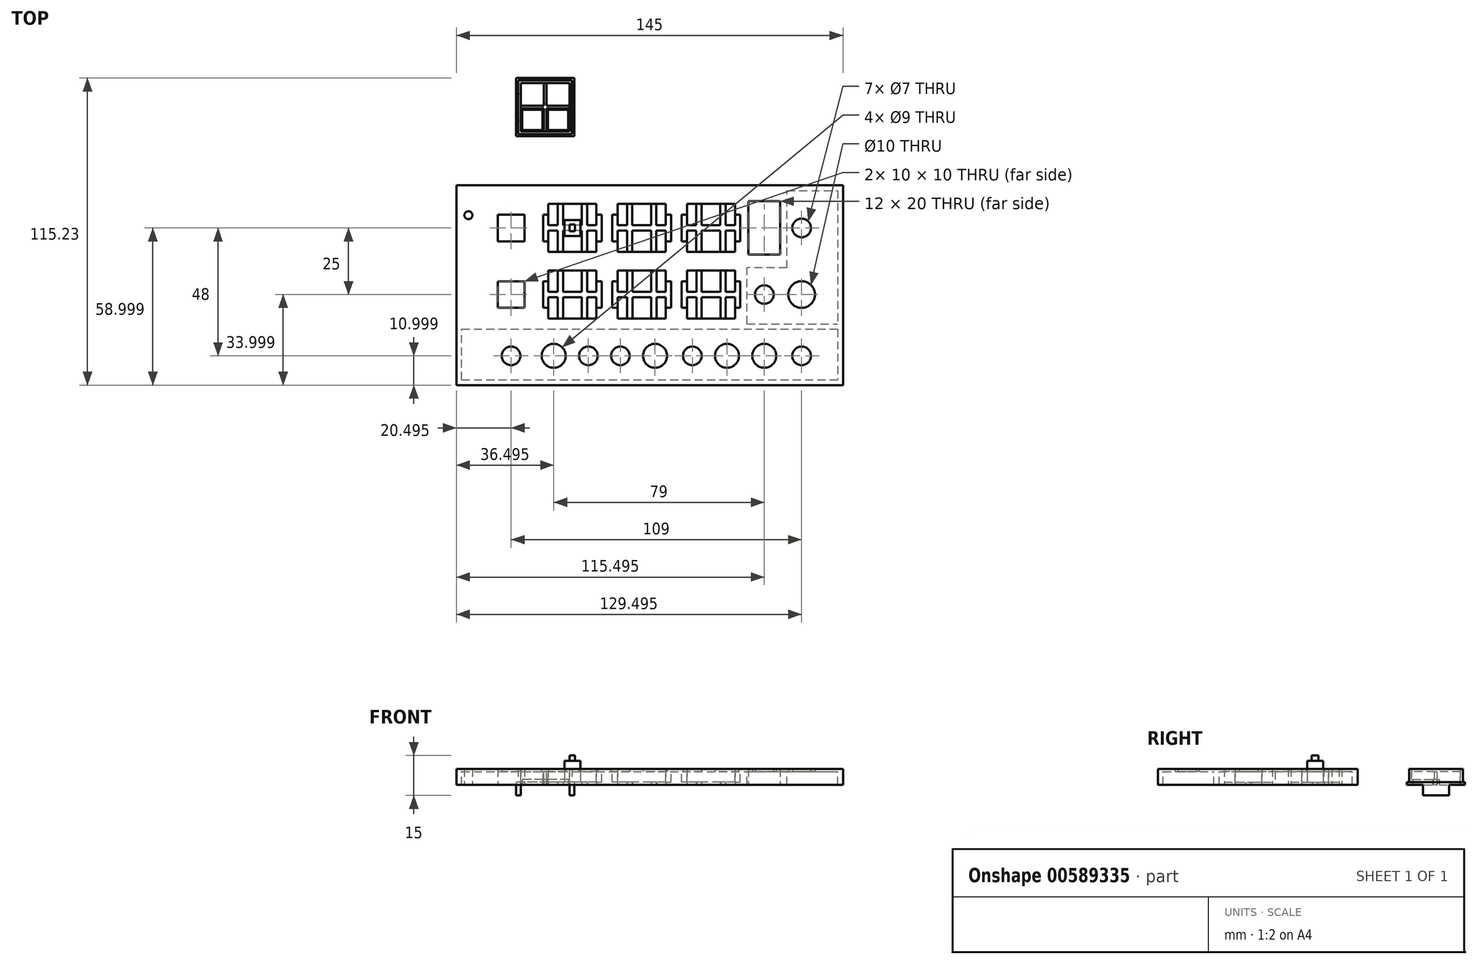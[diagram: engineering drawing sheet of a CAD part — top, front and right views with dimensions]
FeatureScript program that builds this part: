
annotation { "Feature Type Name" : "Feature", "Feature Type Description" : "" }
export const myFeature = defineFeature(function(context is Context, id is Id, definition is map)
    precondition{}
    {
        {
            var Q0;
            Q0=qCreatedBy(makeId("Top.planeOp"),FACE);
            var sketch = newSketch(context, id + "F0", { "sketchPlane" : qUnion([Q0])});
            skLineSegment(sketch, "E0.bottom", {"start": v(-10, -55.04) * mm, "end": v(-155, -55.04) * mm});
            skLineSegment(sketch, "E0.top", {"start": v(-10, 19.96) * mm, "end": v(-155, 19.96) * mm});
            skLineSegment(sketch, "E0.left", {"start": v(-10, -55.04) * mm, "end": v(-10, 19.96) * mm});
            skLineSegment(sketch, "E0.right", {"start": v(-155, -55.04) * mm, "end": v(-155, 19.96) * mm});
            skPoint(sketch, "E0.middle", {"position": v(-82.5, -17.54) * mm});
            skLineSegment(sketch, "E1.bottom", {"start": v(-101.5, -6.04) * mm, "end": v(-121.5, -6.04) * mm, "construction": true});
            skLineSegment(sketch, "E1.top", {"start": v(-101.5, 13.96) * mm, "end": v(-121.5, 13.96) * mm, "construction": true});
            skLineSegment(sketch, "E1.left", {"start": v(-101.5, -6.04) * mm, "end": v(-101.5, 13.96) * mm, "construction": true});
            skLineSegment(sketch, "E1.right", {"start": v(-121.5, -6.04) * mm, "end": v(-121.5, 13.96) * mm, "construction": true});
            skPoint(sketch, "E1.middle", {"position": v(-111.5, 3.96) * mm});
            skLineSegment(sketch, "E2.1.0.0", {"start": v(-95.5, -6.04) * mm, "end": v(-95.5, 13.96) * mm, "construction": true});
            skPoint(sketch, "E2.1.0.1", {"position": v(-85.5, 3.96) * mm});
            skLineSegment(sketch, "E2.1.0.2", {"start": v(-75.5, -6.04) * mm, "end": v(-95.5, -6.04) * mm, "construction": true});
            skLineSegment(sketch, "E2.1.0.3", {"start": v(-75.5, -6.04) * mm, "end": v(-75.5, 13.96) * mm, "construction": true});
            skLineSegment(sketch, "E2.1.0.4", {"start": v(-75.5, 13.96) * mm, "end": v(-95.5, 13.96) * mm, "construction": true});
            skLineSegment(sketch, "E2.2.0.0", {"start": v(-69.5, -6.04) * mm, "end": v(-69.5, 13.96) * mm, "construction": true});
            skPoint(sketch, "E2.2.0.1", {"position": v(-59.5, 3.96) * mm});
            skLineSegment(sketch, "E2.2.0.2", {"start": v(-49.5, -6.04) * mm, "end": v(-69.5, -6.04) * mm, "construction": true});
            skLineSegment(sketch, "E2.2.0.3", {"start": v(-49.5, -6.04) * mm, "end": v(-49.5, 13.96) * mm, "construction": true});
            skLineSegment(sketch, "E2.2.0.4", {"start": v(-49.5, 13.96) * mm, "end": v(-69.5, 13.96) * mm, "construction": true});
            skLineSegment(sketch, "E2.direction1", {"start": v(-121.5, -6.04) * mm, "end": v(-95.5, -6.04) * mm, "construction": true});
            skLineSegment(sketch, "E3.bottom", {"start": v(-101.5, -31.04) * mm, "end": v(-121.5, -31.04) * mm, "construction": true});
            skLineSegment(sketch, "E3.top", {"start": v(-101.5, -11.04) * mm, "end": v(-121.5, -11.04) * mm, "construction": true});
            skLineSegment(sketch, "E3.left", {"start": v(-101.5, -31.04) * mm, "end": v(-101.5, -11.04) * mm, "construction": true});
            skLineSegment(sketch, "E3.right", {"start": v(-121.5, -31.04) * mm, "end": v(-121.5, -11.04) * mm, "construction": true});
            skPoint(sketch, "E3.middle", {"position": v(-111.5, -21.04) * mm});
            skLineSegment(sketch, "E4.1.0.0", {"start": v(-75.5, -31.04) * mm, "end": v(-95.5, -31.04) * mm, "construction": true});
            skLineSegment(sketch, "E4.1.0.1", {"start": v(-75.5, -31.04) * mm, "end": v(-75.5, -11.04) * mm, "construction": true});
            skLineSegment(sketch, "E4.1.0.2", {"start": v(-95.5, -31.04) * mm, "end": v(-95.5, -11.04) * mm, "construction": true});
            skLineSegment(sketch, "E4.1.0.3", {"start": v(-75.5, -11.04) * mm, "end": v(-95.5, -11.04) * mm, "construction": true});
            skPoint(sketch, "E4.1.0.4", {"position": v(-85.5, -21.04) * mm});
            skLineSegment(sketch, "E4.2.0.0", {"start": v(-49.5, -31.04) * mm, "end": v(-69.5, -31.04) * mm, "construction": true});
            skLineSegment(sketch, "E4.2.0.1", {"start": v(-49.5, -31.04) * mm, "end": v(-49.5, -11.04) * mm, "construction": true});
            skLineSegment(sketch, "E4.2.0.2", {"start": v(-69.5, -31.04) * mm, "end": v(-69.5, -11.04) * mm, "construction": true});
            skLineSegment(sketch, "E4.2.0.3", {"start": v(-49.5, -11.04) * mm, "end": v(-69.5, -11.04) * mm, "construction": true});
            skPoint(sketch, "E4.2.0.4", {"position": v(-59.5, -21.04) * mm});
            skLineSegment(sketch, "E4.direction1", {"start": v(-121.5, -31.04) * mm, "end": v(-95.5, -31.04) * mm, "construction": true});
            skCircle(sketch, "E5", {"center": v(-134.5, -44.04) * mm, "radius": 3.5 * mm});
            skCircle(sketch, "E6", {"center": v(-105.5, -44.04) * mm, "radius": 3.5 * mm});
            skCircle(sketch, "E7", {"center": v(-93.5, -44.04) * mm, "radius": 3.5 * mm});
            skLineSegment(sketch, "E8.bottom", {"start": v(-155, 19.96) * mm, "end": v(-147, 19.96) * mm, "construction": true});
            skLineSegment(sketch, "E8.top", {"start": v(-155, -55.04) * mm, "end": v(-147, -55.04) * mm, "construction": true});
            skLineSegment(sketch, "E8.left", {"start": v(-155, 19.96) * mm, "end": v(-155, -55.04) * mm, "construction": true});
            skLineSegment(sketch, "E8.right", {"start": v(-147, 19.96) * mm, "end": v(-147, -55.04) * mm, "construction": true});
            skLineSegment(sketch, "E9.bottom", {"start": v(-10, -55.04) * mm, "end": v(-18, -55.04) * mm, "construction": true});
            skLineSegment(sketch, "E9.top", {"start": v(-10, 19.96) * mm, "end": v(-18, 19.96) * mm, "construction": true});
            skLineSegment(sketch, "E9.left", {"start": v(-10, -55.04) * mm, "end": v(-10, 19.96) * mm, "construction": true});
            skLineSegment(sketch, "E9.right", {"start": v(-18, -55.04) * mm, "end": v(-18, 19.96) * mm, "construction": true});
            skCircle(sketch, "E10", {"center": v(-118.5, -44.04) * mm, "radius": 4.5 * mm});
            skCircle(sketch, "E11", {"center": v(-80.5, -44.04) * mm, "radius": 4.5 * mm});
            skCircle(sketch, "E12", {"center": v(-66.5, -44.04) * mm, "radius": 3.5 * mm});
            skCircle(sketch, "E13", {"center": v(-53.5, -44.04) * mm, "radius": 4.5 * mm});
            skCircle(sketch, "E14", {"center": v(-39.5, -44.04) * mm, "radius": 4.5 * mm});
            skCircle(sketch, "E15", {"center": v(-25.5, -44.04) * mm, "radius": 3.5 * mm});
            skCircle(sketch, "E16", {"center": v(-39.5, -21.04) * mm, "radius": 3.5 * mm});
            skLineSegment(sketch, "E17.bottom", {"start": v(-33.5, -6.04) * mm, "end": v(-45.5, -6.04) * mm});
            skLineSegment(sketch, "E17.top", {"start": v(-33.5, 13.96) * mm, "end": v(-45.5, 13.96) * mm});
            skLineSegment(sketch, "E17.left", {"start": v(-33.5, -6.04) * mm, "end": v(-33.5, 13.96) * mm});
            skLineSegment(sketch, "E17.right", {"start": v(-45.5, -6.04) * mm, "end": v(-45.5, 13.96) * mm});
            skPoint(sketch, "E17.middle", {"position": v(-39.5, 3.96) * mm});
            skCircle(sketch, "E18", {"center": v(-25.5, 3.96) * mm, "radius": 3.5 * mm});
            skCircle(sketch, "E19", {"center": v(-25.5, -21.04) * mm, "radius": 5 * mm});
            skPoint(sketch, "E20.centerSnap0", {"position": v(-121.5, -21.04) * mm});
            skLineSegment(sketch, "E21.bottom", {"start": v(-102.5, -5.04) * mm, "end": v(-120.5, -5.04) * mm});
            skLineSegment(sketch, "E21.top", {"start": v(-102.5, 12.96) * mm, "end": v(-120.5, 12.96) * mm});
            skLineSegment(sketch, "E21.left", {"start": v(-102.5, -5.04) * mm, "end": v(-102.5, 12.96) * mm});
            skLineSegment(sketch, "E21.right", {"start": v(-120.5, -5.04) * mm, "end": v(-120.5, 12.96) * mm});
            skLineSegment(sketch, "E22.bottom", {"start": v(-102.5, -30.04) * mm, "end": v(-120.5, -30.04) * mm});
            skLineSegment(sketch, "E22.top", {"start": v(-102.5, -12.04) * mm, "end": v(-120.5, -12.04) * mm});
            skLineSegment(sketch, "E22.left", {"start": v(-102.5, -30.04) * mm, "end": v(-102.5, -12.04) * mm});
            skLineSegment(sketch, "E22.right", {"start": v(-120.5, -30.04) * mm, "end": v(-120.5, -12.04) * mm});
            skLineSegment(sketch, "E23.bottom", {"start": v(-102.5, 2.96) * mm, "end": v(-106, 2.96) * mm});
            skLineSegment(sketch, "E23.top", {"start": v(-102.5, 4.96) * mm, "end": v(-106, 4.96) * mm});
            skLineSegment(sketch, "E23.left", {"start": v(-102.5, 2.96) * mm, "end": v(-102.5, 4.96) * mm});
            skLineSegment(sketch, "E23.right", {"start": v(-120.5, 2.96) * mm, "end": v(-120.5, 4.96) * mm});
            skLineSegment(sketch, "E24.bottom", {"start": v(-115, -5.04) * mm, "end": v(-117, -5.04) * mm});
            skLineSegment(sketch, "E24.top", {"start": v(-115, 12.96) * mm, "end": v(-117, 12.96) * mm});
            skLineSegment(sketch, "E24.left", {"start": v(-115, -5.04) * mm, "end": v(-115, 2.96) * mm});
            skLineSegment(sketch, "E24.right", {"start": v(-117, -5.04) * mm, "end": v(-117, 2.96) * mm});
            skPoint(sketch, "E24.middle", {"position": v(-116, 3.96) * mm});
            skLineSegment(sketch, "E25.bottom", {"start": v(-106, -5.04) * mm, "end": v(-108, -5.04) * mm});
            skLineSegment(sketch, "E25.top", {"start": v(-106, 12.96) * mm, "end": v(-108, 12.96) * mm});
            skLineSegment(sketch, "E25.left", {"start": v(-106, -5.04) * mm, "end": v(-106, 2.96) * mm});
            skLineSegment(sketch, "E25.right", {"start": v(-108, -5.04) * mm, "end": v(-108, 2.96) * mm});
            skPoint(sketch, "E25.middle", {"position": v(-107, 3.96) * mm});
            skLineSegment(sketch, "E26.trimOffspring", {"start": v(-117, 4.96) * mm, "end": v(-117, 12.96) * mm});
            skLineSegment(sketch, "E27.trimOffspring", {"start": v(-117, 4.96) * mm, "end": v(-120.5, 4.96) * mm});
            skLineSegment(sketch, "E28.trimOffspring", {"start": v(-115, 4.96) * mm, "end": v(-115, 12.96) * mm});
            skLineSegment(sketch, "E29.trimOffspring", {"start": v(-117, 2.96) * mm, "end": v(-120.5, 2.96) * mm});
            skLineSegment(sketch, "E30.trimOffspring", {"start": v(-108, 4.96) * mm, "end": v(-108, 12.96) * mm});
            skLineSegment(sketch, "E31.trimOffspring", {"start": v(-108, 4.96) * mm, "end": v(-115, 4.96) * mm});
            skLineSegment(sketch, "E32.trimOffspring", {"start": v(-106, 4.96) * mm, "end": v(-106, 12.96) * mm});
            skLineSegment(sketch, "E33.trimOffspring", {"start": v(-108, 2.96) * mm, "end": v(-115, 2.96) * mm});
            skLineSegment(sketch, "E34.bottom", {"start": v(-131, -50.54) * mm, "end": v(-138, -50.54) * mm, "construction": true});
            skLineSegment(sketch, "E34.top", {"start": v(-131, -37.54) * mm, "end": v(-138, -37.54) * mm, "construction": true});
            skLineSegment(sketch, "E34.left", {"start": v(-131, -50.54) * mm, "end": v(-131, -37.54) * mm, "construction": true});
            skLineSegment(sketch, "E34.right", {"start": v(-138, -50.54) * mm, "end": v(-138, -37.54) * mm, "construction": true});
            skLineSegment(sketch, "E35.bottom", {"start": v(-102.5, -22.04) * mm, "end": v(-105.98, -22.04) * mm});
            skLineSegment(sketch, "E35.top", {"start": v(-102.5, -20.04) * mm, "end": v(-105.98, -20.04) * mm});
            skLineSegment(sketch, "E35.left", {"start": v(-102.5, -22.04) * mm, "end": v(-102.5, -20.04) * mm});
            skLineSegment(sketch, "E35.right", {"start": v(-120.5, -22.04) * mm, "end": v(-120.5, -20.04) * mm});
            skLineSegment(sketch, "E36.bottom", {"start": v(-114.98, -30.04) * mm, "end": v(-116.98, -30.04) * mm});
            skLineSegment(sketch, "E36.top", {"start": v(-114.98, -12.04) * mm, "end": v(-116.98, -12.04) * mm});
            skLineSegment(sketch, "E36.left", {"start": v(-114.98, -30.04) * mm, "end": v(-114.98, -22.04) * mm});
            skLineSegment(sketch, "E36.right", {"start": v(-116.98, -30.04) * mm, "end": v(-116.98, -22.04) * mm});
            skPoint(sketch, "E36.middle", {"position": v(-115.98, -21.04) * mm});
            skLineSegment(sketch, "E37.bottom", {"start": v(-105.98, -30.04) * mm, "end": v(-107.98, -30.04) * mm});
            skLineSegment(sketch, "E37.top", {"start": v(-105.98, -12.04) * mm, "end": v(-107.98, -12.04) * mm});
            skLineSegment(sketch, "E37.left", {"start": v(-105.98, -30.04) * mm, "end": v(-105.98, -22.04) * mm});
            skLineSegment(sketch, "E37.right", {"start": v(-107.98, -30.04) * mm, "end": v(-107.98, -22.04) * mm});
            skPoint(sketch, "E37.middle", {"position": v(-106.98, -21.04) * mm});
            skLineSegment(sketch, "E38.trimOffspring", {"start": v(-116.98, -20.04) * mm, "end": v(-116.98, -12.04) * mm});
            skLineSegment(sketch, "E39.trimOffspring", {"start": v(-116.98, -20.04) * mm, "end": v(-120.5, -20.04) * mm});
            skLineSegment(sketch, "E40.trimOffspring", {"start": v(-114.98, -20.04) * mm, "end": v(-114.98, -12.04) * mm});
            skLineSegment(sketch, "E41.trimOffspring", {"start": v(-116.98, -22.04) * mm, "end": v(-120.5, -22.04) * mm});
            skLineSegment(sketch, "E42.trimOffspring", {"start": v(-107.98, -20.04) * mm, "end": v(-107.98, -12.04) * mm});
            skLineSegment(sketch, "E43.trimOffspring", {"start": v(-107.98, -20.04) * mm, "end": v(-114.98, -20.04) * mm});
            skLineSegment(sketch, "E44.trimOffspring", {"start": v(-105.98, -20.04) * mm, "end": v(-105.98, -12.04) * mm});
            skLineSegment(sketch, "E45.trimOffspring", {"start": v(-107.98, -22.04) * mm, "end": v(-114.98, -22.04) * mm});
            skLineSegment(sketch, "E46.bottom", {"start": v(-129.5, -1.04) * mm, "end": v(-139.5, -1.04) * mm});
            skLineSegment(sketch, "E46.top", {"start": v(-129.5, 8.96) * mm, "end": v(-139.5, 8.96) * mm});
            skLineSegment(sketch, "E46.left", {"start": v(-129.5, -1.04) * mm, "end": v(-129.5, 8.96) * mm});
            skLineSegment(sketch, "E46.right", {"start": v(-139.5, -1.04) * mm, "end": v(-139.5, 8.96) * mm});
            skPoint(sketch, "E46.middle", {"position": v(-134.5, 3.96) * mm});
            skLineSegment(sketch, "E47.bottom", {"start": v(-129.5, -26.04) * mm, "end": v(-139.5, -26.04) * mm});
            skLineSegment(sketch, "E47.top", {"start": v(-129.5, -16.04) * mm, "end": v(-139.5, -16.04) * mm});
            skLineSegment(sketch, "E47.left", {"start": v(-129.5, -26.04) * mm, "end": v(-129.5, -16.04) * mm});
            skLineSegment(sketch, "E47.right", {"start": v(-139.5, -26.04) * mm, "end": v(-139.5, -16.04) * mm});
            skPoint(sketch, "E47.middle", {"position": v(-134.5, -21.04) * mm});
            skLineSegment(sketch, "E48.1.0.0", {"start": v(-91, 4.96) * mm, "end": v(-91, 12.96) * mm});
            skLineSegment(sketch, "E48.1.0.2", {"start": v(-76.5, -5.04) * mm, "end": v(-76.5, 12.96) * mm});
            skLineSegment(sketch, "E48.1.0.3", {"start": v(-80, -5.04) * mm, "end": v(-80, 2.96) * mm});
            skPoint(sketch, "E48.1.0.4", {"position": v(-90, 3.96) * mm});
            skLineSegment(sketch, "E48.1.0.5", {"start": v(-82, 4.96) * mm, "end": v(-82, 12.96) * mm});
            skLineSegment(sketch, "E48.1.0.6", {"start": v(-80, 4.96) * mm, "end": v(-80, 12.96) * mm});
            skLineSegment(sketch, "E48.1.0.7", {"start": v(-82, 4.96) * mm, "end": v(-89, 4.96) * mm});
            skLineSegment(sketch, "E48.1.0.8", {"start": v(-76.5, 4.96) * mm, "end": v(-80, 4.96) * mm});
            skLineSegment(sketch, "E48.1.0.9", {"start": v(-76.5, 2.96) * mm, "end": v(-80, 2.96) * mm});
            skLineSegment(sketch, "E48.1.0.10", {"start": v(-80, 12.96) * mm, "end": v(-82, 12.96) * mm});
            skPoint(sketch, "E48.1.0.11", {"position": v(-81, 3.96) * mm});
            skLineSegment(sketch, "E48.1.0.12", {"start": v(-91, 4.96) * mm, "end": v(-94.5, 4.96) * mm});
            skLineSegment(sketch, "E48.1.0.13", {"start": v(-91, 2.96) * mm, "end": v(-94.5, 2.96) * mm});
            skLineSegment(sketch, "E48.1.0.14", {"start": v(-89, 4.96) * mm, "end": v(-89, 12.96) * mm});
            skLineSegment(sketch, "E48.1.0.15", {"start": v(-76.5, 12.96) * mm, "end": v(-94.5, 12.96) * mm});
            skLineSegment(sketch, "E48.1.0.16", {"start": v(-91, -5.04) * mm, "end": v(-91, 2.96) * mm});
            skLineSegment(sketch, "E48.1.0.17", {"start": v(-76.5, -5.04) * mm, "end": v(-94.5, -5.04) * mm});
            skLineSegment(sketch, "E48.1.0.18", {"start": v(-89, -5.04) * mm, "end": v(-89, 2.96) * mm});
            skLineSegment(sketch, "E48.1.0.19", {"start": v(-82, -5.04) * mm, "end": v(-82, 2.96) * mm});
            skLineSegment(sketch, "E48.1.0.20", {"start": v(-94.5, -5.04) * mm, "end": v(-94.5, 12.96) * mm});
            skLineSegment(sketch, "E48.1.0.21", {"start": v(-82, 2.96) * mm, "end": v(-89, 2.96) * mm});
            skLineSegment(sketch, "E48.1.0.22", {"start": v(-80, -5.04) * mm, "end": v(-82, -5.04) * mm});
            skLineSegment(sketch, "E48.1.0.23", {"start": v(-76.5, 2.96) * mm, "end": v(-76.5, 4.96) * mm});
            skLineSegment(sketch, "E48.1.0.24", {"start": v(-89, -5.04) * mm, "end": v(-91, -5.04) * mm});
            skLineSegment(sketch, "E48.1.0.25", {"start": v(-94.5, 2.96) * mm, "end": v(-94.5, 4.96) * mm});
            skLineSegment(sketch, "E48.1.0.27", {"start": v(-89, 12.96) * mm, "end": v(-91, 12.96) * mm});
            skLineSegment(sketch, "E48.2.0.0", {"start": v(-65, 4.96) * mm, "end": v(-65, 12.96) * mm});
            skLineSegment(sketch, "E48.2.0.2", {"start": v(-50.5, -5.04) * mm, "end": v(-50.5, 12.96) * mm});
            skLineSegment(sketch, "E48.2.0.3", {"start": v(-54, -5.04) * mm, "end": v(-54, 2.96) * mm});
            skPoint(sketch, "E48.2.0.4", {"position": v(-64, 3.96) * mm});
            skLineSegment(sketch, "E48.2.0.5", {"start": v(-56, 4.96) * mm, "end": v(-56, 12.96) * mm});
            skLineSegment(sketch, "E48.2.0.6", {"start": v(-54, 4.96) * mm, "end": v(-54, 12.96) * mm});
            skLineSegment(sketch, "E48.2.0.7", {"start": v(-56, 4.96) * mm, "end": v(-63, 4.96) * mm});
            skLineSegment(sketch, "E48.2.0.8", {"start": v(-50.5, 4.96) * mm, "end": v(-54, 4.96) * mm});
            skLineSegment(sketch, "E48.2.0.9", {"start": v(-50.5, 2.96) * mm, "end": v(-54, 2.96) * mm});
            skLineSegment(sketch, "E48.2.0.10", {"start": v(-54, 12.96) * mm, "end": v(-56, 12.96) * mm});
            skPoint(sketch, "E48.2.0.11", {"position": v(-55, 3.96) * mm});
            skLineSegment(sketch, "E48.2.0.12", {"start": v(-65, 4.96) * mm, "end": v(-68.5, 4.96) * mm});
            skLineSegment(sketch, "E48.2.0.13", {"start": v(-65, 2.96) * mm, "end": v(-68.5, 2.96) * mm});
            skLineSegment(sketch, "E48.2.0.14", {"start": v(-63, 4.96) * mm, "end": v(-63, 12.96) * mm});
            skLineSegment(sketch, "E48.2.0.15", {"start": v(-50.5, 12.96) * mm, "end": v(-68.5, 12.96) * mm});
            skLineSegment(sketch, "E48.2.0.16", {"start": v(-65, -5.04) * mm, "end": v(-65, 2.96) * mm});
            skLineSegment(sketch, "E48.2.0.17", {"start": v(-50.5, -5.04) * mm, "end": v(-68.5, -5.04) * mm});
            skLineSegment(sketch, "E48.2.0.18", {"start": v(-63, -5.04) * mm, "end": v(-63, 2.96) * mm});
            skLineSegment(sketch, "E48.2.0.19", {"start": v(-56, -5.04) * mm, "end": v(-56, 2.96) * mm});
            skLineSegment(sketch, "E48.2.0.20", {"start": v(-68.5, -5.04) * mm, "end": v(-68.5, 12.96) * mm});
            skLineSegment(sketch, "E48.2.0.21", {"start": v(-56, 2.96) * mm, "end": v(-63, 2.96) * mm});
            skLineSegment(sketch, "E48.2.0.22", {"start": v(-54, -5.04) * mm, "end": v(-56, -5.04) * mm});
            skLineSegment(sketch, "E48.2.0.23", {"start": v(-50.5, 2.96) * mm, "end": v(-50.5, 4.96) * mm});
            skLineSegment(sketch, "E48.2.0.24", {"start": v(-63, -5.04) * mm, "end": v(-65, -5.04) * mm});
            skLineSegment(sketch, "E48.2.0.25", {"start": v(-68.5, 2.96) * mm, "end": v(-68.5, 4.96) * mm});
            skLineSegment(sketch, "E48.2.0.27", {"start": v(-63, 12.96) * mm, "end": v(-65, 12.96) * mm});
            skLineSegment(sketch, "E48.direction1", {"start": v(-120.5, -5.04) * mm, "end": v(-94.5, -5.04) * mm, "construction": true});
            skLineSegment(sketch, "E49.1.0.0", {"start": v(-76.5, -20.04) * mm, "end": v(-79.98, -20.04) * mm});
            skLineSegment(sketch, "E49.1.0.1", {"start": v(-88.98, -20.04) * mm, "end": v(-88.98, -12.04) * mm});
            skLineSegment(sketch, "E49.1.0.2", {"start": v(-81.98, -30.04) * mm, "end": v(-81.98, -22.04) * mm});
            skLineSegment(sketch, "E49.1.0.3", {"start": v(-94.5, -30.04) * mm, "end": v(-94.5, -12.04) * mm});
            skLineSegment(sketch, "E49.1.0.4", {"start": v(-90.98, -30.04) * mm, "end": v(-90.98, -22.04) * mm});
            skLineSegment(sketch, "E49.1.0.5", {"start": v(-76.5, -30.04) * mm, "end": v(-76.5, -12.04) * mm});
            skLineSegment(sketch, "E49.1.0.6", {"start": v(-81.98, -22.04) * mm, "end": v(-88.98, -22.04) * mm});
            skLineSegment(sketch, "E49.1.0.7", {"start": v(-88.98, -30.04) * mm, "end": v(-88.98, -22.04) * mm});
            skLineSegment(sketch, "E49.1.0.9", {"start": v(-79.98, -20.04) * mm, "end": v(-79.98, -12.04) * mm});
            skLineSegment(sketch, "E49.1.0.10", {"start": v(-76.5, -22.04) * mm, "end": v(-79.98, -22.04) * mm});
            skPoint(sketch, "E49.1.0.11", {"position": v(-80.98, -21.04) * mm});
            skLineSegment(sketch, "E49.1.0.12", {"start": v(-90.98, -22.04) * mm, "end": v(-94.5, -22.04) * mm});
            skLineSegment(sketch, "E49.1.0.14", {"start": v(-81.98, -20.04) * mm, "end": v(-88.98, -20.04) * mm});
            skPoint(sketch, "E49.1.0.15", {"position": v(-89.98, -21.04) * mm});
            skLineSegment(sketch, "E49.1.0.16", {"start": v(-79.98, -30.04) * mm, "end": v(-79.98, -22.04) * mm});
            skLineSegment(sketch, "E49.1.0.17", {"start": v(-76.5, -30.04) * mm, "end": v(-94.5, -30.04) * mm});
            skLineSegment(sketch, "E49.1.0.18", {"start": v(-90.98, -20.04) * mm, "end": v(-90.98, -12.04) * mm});
            skLineSegment(sketch, "E49.1.0.19", {"start": v(-81.98, -20.04) * mm, "end": v(-81.98, -12.04) * mm});
            skLineSegment(sketch, "E49.1.0.20", {"start": v(-90.98, -20.04) * mm, "end": v(-94.5, -20.04) * mm});
            skLineSegment(sketch, "E49.1.0.21", {"start": v(-76.5, -12.04) * mm, "end": v(-94.5, -12.04) * mm});
            skLineSegment(sketch, "E49.1.0.22", {"start": v(-88.98, -12.04) * mm, "end": v(-90.98, -12.04) * mm});
            skLineSegment(sketch, "E49.1.0.23", {"start": v(-76.5, -22.04) * mm, "end": v(-76.5, -20.04) * mm});
            skLineSegment(sketch, "E49.1.0.24", {"start": v(-94.5, -22.04) * mm, "end": v(-94.5, -20.04) * mm});
            skLineSegment(sketch, "E49.1.0.26", {"start": v(-94.5, -30.04) * mm, "end": v(-94.5, -12.04) * mm});
            skLineSegment(sketch, "E49.1.0.27", {"start": v(-79.98, -12.04) * mm, "end": v(-81.98, -12.04) * mm});
            skLineSegment(sketch, "E49.1.0.28", {"start": v(-76.5, -30.04) * mm, "end": v(-94.5, -30.04) * mm});
            skLineSegment(sketch, "E49.1.0.29", {"start": v(-76.5, -12.04) * mm, "end": v(-94.5, -12.04) * mm});
            skLineSegment(sketch, "E49.1.0.30", {"start": v(-76.5, -30.04) * mm, "end": v(-76.5, -12.04) * mm});
            skLineSegment(sketch, "E49.1.0.31", {"start": v(-88.98, -30.04) * mm, "end": v(-90.98, -30.04) * mm});
            skLineSegment(sketch, "E49.1.0.32", {"start": v(-79.98, -30.04) * mm, "end": v(-81.98, -30.04) * mm});
            skLineSegment(sketch, "E49.2.0.0", {"start": v(-50.5, -20.04) * mm, "end": v(-53.98, -20.04) * mm});
            skLineSegment(sketch, "E49.2.0.1", {"start": v(-62.98, -20.04) * mm, "end": v(-62.98, -12.04) * mm});
            skLineSegment(sketch, "E49.2.0.2", {"start": v(-55.98, -30.04) * mm, "end": v(-55.98, -22.04) * mm});
            skLineSegment(sketch, "E49.2.0.3", {"start": v(-68.5, -30.04) * mm, "end": v(-68.5, -12.04) * mm});
            skLineSegment(sketch, "E49.2.0.4", {"start": v(-64.98, -30.04) * mm, "end": v(-64.98, -22.04) * mm});
            skLineSegment(sketch, "E49.2.0.5", {"start": v(-50.5, -30.04) * mm, "end": v(-50.5, -12.04) * mm});
            skLineSegment(sketch, "E49.2.0.6", {"start": v(-55.98, -22.04) * mm, "end": v(-62.98, -22.04) * mm});
            skLineSegment(sketch, "E49.2.0.7", {"start": v(-62.98, -30.04) * mm, "end": v(-62.98, -22.04) * mm});
            skLineSegment(sketch, "E49.2.0.9", {"start": v(-53.98, -20.04) * mm, "end": v(-53.98, -12.04) * mm});
            skLineSegment(sketch, "E49.2.0.10", {"start": v(-50.5, -22.04) * mm, "end": v(-53.98, -22.04) * mm});
            skPoint(sketch, "E49.2.0.11", {"position": v(-54.98, -21.04) * mm});
            skLineSegment(sketch, "E49.2.0.12", {"start": v(-64.98, -22.04) * mm, "end": v(-68.5, -22.04) * mm});
            skLineSegment(sketch, "E49.2.0.14", {"start": v(-55.98, -20.04) * mm, "end": v(-62.98, -20.04) * mm});
            skPoint(sketch, "E49.2.0.15", {"position": v(-63.98, -21.04) * mm});
            skLineSegment(sketch, "E49.2.0.16", {"start": v(-53.98, -30.04) * mm, "end": v(-53.98, -22.04) * mm});
            skLineSegment(sketch, "E49.2.0.17", {"start": v(-50.5, -30.04) * mm, "end": v(-68.5, -30.04) * mm});
            skLineSegment(sketch, "E49.2.0.18", {"start": v(-64.98, -20.04) * mm, "end": v(-64.98, -12.04) * mm});
            skLineSegment(sketch, "E49.2.0.19", {"start": v(-55.98, -20.04) * mm, "end": v(-55.98, -12.04) * mm});
            skLineSegment(sketch, "E49.2.0.20", {"start": v(-64.98, -20.04) * mm, "end": v(-68.5, -20.04) * mm});
            skLineSegment(sketch, "E49.2.0.21", {"start": v(-50.5, -12.04) * mm, "end": v(-68.5, -12.04) * mm});
            skLineSegment(sketch, "E49.2.0.22", {"start": v(-62.98, -12.04) * mm, "end": v(-64.98, -12.04) * mm});
            skLineSegment(sketch, "E49.2.0.23", {"start": v(-50.5, -22.04) * mm, "end": v(-50.5, -20.04) * mm});
            skLineSegment(sketch, "E49.2.0.24", {"start": v(-68.5, -22.04) * mm, "end": v(-68.5, -20.04) * mm});
            skLineSegment(sketch, "E49.2.0.26", {"start": v(-68.5, -30.04) * mm, "end": v(-68.5, -12.04) * mm});
            skLineSegment(sketch, "E49.2.0.27", {"start": v(-53.98, -12.04) * mm, "end": v(-55.98, -12.04) * mm});
            skLineSegment(sketch, "E49.2.0.28", {"start": v(-50.5, -30.04) * mm, "end": v(-68.5, -30.04) * mm});
            skLineSegment(sketch, "E49.2.0.29", {"start": v(-50.5, -12.04) * mm, "end": v(-68.5, -12.04) * mm});
            skLineSegment(sketch, "E49.2.0.30", {"start": v(-50.5, -30.04) * mm, "end": v(-50.5, -12.04) * mm});
            skLineSegment(sketch, "E49.2.0.31", {"start": v(-62.98, -30.04) * mm, "end": v(-64.98, -30.04) * mm});
            skLineSegment(sketch, "E49.2.0.32", {"start": v(-53.98, -30.04) * mm, "end": v(-55.98, -30.04) * mm});
            skLineSegment(sketch, "E49.direction1", {"start": v(-120.5, -30.04) * mm, "end": v(-94.5, -30.04) * mm, "construction": true});
            skLineSegment(sketch, "E50.bottom", {"start": v(-133.5, -1.04) * mm, "end": v(-135.5, -1.04) * mm});
            skLineSegment(sketch, "E50.top", {"start": v(-133.5, 8.96) * mm, "end": v(-135.5, 8.96) * mm});
            skLineSegment(sketch, "E50.left", {"start": v(-133.5, -1.04) * mm, "end": v(-133.5, 8.96) * mm});
            skLineSegment(sketch, "E50.right", {"start": v(-135.5, -1.04) * mm, "end": v(-135.5, 8.96) * mm});
            skLineSegment(sketch, "E51.bottom", {"start": v(-133.5, -26.04) * mm, "end": v(-135.5, -26.04) * mm});
            skLineSegment(sketch, "E51.top", {"start": v(-133.5, -16.04) * mm, "end": v(-135.5, -16.04) * mm});
            skLineSegment(sketch, "E51.left", {"start": v(-133.5, -26.04) * mm, "end": v(-133.5, -16.04) * mm});
            skLineSegment(sketch, "E51.right", {"start": v(-135.5, -26.04) * mm, "end": v(-135.5, -16.04) * mm});
            skCircle(sketch, "E52", {"center": v(-150.5, 8.76) * mm, "radius": 1.5 * mm});
            skPoint(sketch, "E52.centerSnap0", {"position": v(-151, 19.96) * mm});
            skSolve(sketch);
        }
        {
            var Q0;
            Q0=makeQuery(id+"F0.imprint","IMPRINT",FACE,{"disambiguationData":[TD([[makeQuery(id+"F0.imprint","IMPRINT",EDGE,{"derivedFrom":sQuery(id+"F0.wireOp",EDGE,"E0.bottom")}),-1.0]])]});
            var Q1;
            Q1=makeQuery(id+"F0.imprint","IMPRINT",FACE,{"disambiguationData":[TD([[makeQuery(id+"F0.imprint","IMPRINT",EDGE,{"derivedFrom":sQuery(id+"F0.wireOp",EDGE,"E23.bottom")}),-1.0]])]});
            var Q2;
            Q2=makeQuery(id+"F0.imprint","IMPRINT",FACE,{"disambiguationData":[TD([[makeQuery(id+"F0.imprint","IMPRINT",EDGE,{"derivedFrom":sQuery(id+"F0.wireOp",EDGE,"E35.bottom")}),-1.0]])]});
            var Q3;
            Q3=makeQuery(id+"F0.imprint","IMPRINT",FACE,{"disambiguationData":[TD([[makeQuery(id+"F0.imprint","IMPRINT",EDGE,{"derivedFrom":sQuery(id+"F0.wireOp",EDGE,"E48.1.0.0")}),-1.0]])]});
            var Q4;
            Q4=makeQuery(id+"F0.imprint","IMPRINT",FACE,{"disambiguationData":[TD([[makeQuery(id+"F0.imprint","IMPRINT",EDGE,{"derivedFrom":sQuery(id+"F0.wireOp",EDGE,"E48.2.0.0")}),-1.0]])]});
            var Q5;
            {var subQ3=sQuery(id+"F0.wireOp",EDGE,"E49.2.0.0");Q5=makeQuery(id+"F0.imprint","IMPRINT",FACE,{"disambiguationData":[TD([[makeQuery(id+"F0.imprint","IMPRINT",EDGE,{"derivedFrom":subQ3}),1.0]])]});}
            var Q6;
            {var subQ3=sQuery(id+"F0.wireOp",EDGE,"E49.1.0.0");Q6=makeQuery(id+"F0.imprint","IMPRINT",FACE,{"disambiguationData":[TD([[makeQuery(id+"F0.imprint","IMPRINT",EDGE,{"derivedFrom":subQ3}),1.0]])]});}
            var Q7;
            Q7=makeQuery(id+"F0.imprint","IMPRINT",FACE,{"disambiguationData":[TD([[makeQuery(id+"F0.imprint","IMPRINT",EDGE,{"derivedFrom":sQuery(id+"F0.wireOp",EDGE,"E50.bottom")}),-1.0]])]});
            var Q8;
            Q8=makeQuery(id+"F0.imprint","IMPRINT",FACE,{"disambiguationData":[TD([[makeQuery(id+"F0.imprint","IMPRINT",EDGE,{"derivedFrom":sQuery(id+"F0.wireOp",EDGE,"E51.bottom")}),-1.0]])]});
            extrude(context, id + "F1", {"entities" : qUnion([Q0, Q1, Q2, Q3, Q4, Q5, Q6, Q7, Q8]), "depth" : 1 * mm});
        }
        {
            var Q0;
            Q0=makeQuery(id+"F1.opExtrude","CAP_FACE",FACE,{"disambiguationData":[OSD([sQuery(id+"F0.wireOp",EDGE,"E0.bottom"),sQuery(id+"F0.wireOp",EDGE,"E0.top"),sQuery(id+"F0.wireOp",EDGE,"E0.left"),sQuery(id+"F0.wireOp",EDGE,"E0.right"),sQuery(id+"F0.wireOp",EDGE,"E5"),sQuery(id+"F0.wireOp",EDGE,"E6"),sQuery(id+"F0.wireOp",EDGE,"E7"),sQuery(id+"F0.wireOp",EDGE,"E10"),sQuery(id+"F0.wireOp",EDGE,"E11"),sQuery(id+"F0.wireOp",EDGE,"E12"),sQuery(id+"F0.wireOp",EDGE,"E13"),sQuery(id+"F0.wireOp",EDGE,"E14"),sQuery(id+"F0.wireOp",EDGE,"E15"),sQuery(id+"F0.wireOp",EDGE,"E16"),sQuery(id+"F0.wireOp",EDGE,"E17.bottom"),sQuery(id+"F0.wireOp",EDGE,"E17.top"),sQuery(id+"F0.wireOp",EDGE,"E17.left"),sQuery(id+"F0.wireOp",EDGE,"E17.right"),sQuery(id+"F0.wireOp",EDGE,"E18"),sQuery(id+"F0.wireOp",EDGE,"E19"),sQuery(id+"F0.wireOp",EDGE,"E21.bottom"),sQuery(id+"F0.wireOp",EDGE,"E21.top"),sQuery(id+"F0.wireOp",EDGE,"E21.left"),sQuery(id+"F0.wireOp",EDGE,"E21.right"),sQuery(id+"F0.wireOp",EDGE,"E23.bottom"),sQuery(id+"F0.wireOp",EDGE,"E23.top"),sQuery(id+"F0.wireOp",EDGE,"E24.left"),sQuery(id+"F0.wireOp",EDGE,"E24.right"),sQuery(id+"F0.wireOp",EDGE,"E25.left"),sQuery(id+"F0.wireOp",EDGE,"E25.right"),sQuery(id+"F0.wireOp",EDGE,"E26.trimOffspring"),sQuery(id+"F0.wireOp",EDGE,"E27.trimOffspring"),sQuery(id+"F0.wireOp",EDGE,"E28.trimOffspring"),sQuery(id+"F0.wireOp",EDGE,"E29.trimOffspring"),sQuery(id+"F0.wireOp",EDGE,"E30.trimOffspring"),sQuery(id+"F0.wireOp",EDGE,"E31.trimOffspring"),sQuery(id+"F0.wireOp",EDGE,"E32.trimOffspring"),sQuery(id+"F0.wireOp",EDGE,"E33.trimOffspring"),sQuery(id+"F0.wireOp",EDGE,"E22.bottom"),sQuery(id+"F0.wireOp",EDGE,"E22.top"),sQuery(id+"F0.wireOp",EDGE,"E22.left"),sQuery(id+"F0.wireOp",EDGE,"E22.right"),sQuery(id+"F0.wireOp",EDGE,"E35.bottom"),sQuery(id+"F0.wireOp",EDGE,"E35.top"),sQuery(id+"F0.wireOp",EDGE,"E36.left"),sQuery(id+"F0.wireOp",EDGE,"E36.right"),sQuery(id+"F0.wireOp",EDGE,"E37.left"),sQuery(id+"F0.wireOp",EDGE,"E37.right"),sQuery(id+"F0.wireOp",EDGE,"E38.trimOffspring"),sQuery(id+"F0.wireOp",EDGE,"E39.trimOffspring"),sQuery(id+"F0.wireOp",EDGE,"E40.trimOffspring"),sQuery(id+"F0.wireOp",EDGE,"E41.trimOffspring"),sQuery(id+"F0.wireOp",EDGE,"E42.trimOffspring"),sQuery(id+"F0.wireOp",EDGE,"E43.trimOffspring"),sQuery(id+"F0.wireOp",EDGE,"E44.trimOffspring"),sQuery(id+"F0.wireOp",EDGE,"E45.trimOffspring"),sQuery(id+"F0.wireOp",EDGE,"E46.bottom"),sQuery(id+"F0.wireOp",EDGE,"E46.top"),sQuery(id+"F0.wireOp",EDGE,"E46.left"),sQuery(id+"F0.wireOp",EDGE,"E46.right"),sQuery(id+"F0.wireOp",EDGE,"E47.bottom"),sQuery(id+"F0.wireOp",EDGE,"E47.top"),sQuery(id+"F0.wireOp",EDGE,"E47.left"),sQuery(id+"F0.wireOp",EDGE,"E47.right"),sQuery(id+"F0.wireOp",EDGE,"E48.1.0.0"),sQuery(id+"F0.wireOp",EDGE,"E48.1.0.2"),sQuery(id+"F0.wireOp",EDGE,"E48.1.0.3"),sQuery(id+"F0.wireOp",EDGE,"E48.1.0.5"),sQuery(id+"F0.wireOp",EDGE,"E48.1.0.6"),sQuery(id+"F0.wireOp",EDGE,"E48.1.0.7"),sQuery(id+"F0.wireOp",EDGE,"E48.1.0.8"),sQuery(id+"F0.wireOp",EDGE,"E48.1.0.9"),sQuery(id+"F0.wireOp",EDGE,"E48.1.0.12"),sQuery(id+"F0.wireOp",EDGE,"E48.1.0.13"),sQuery(id+"F0.wireOp",EDGE,"E48.1.0.14"),sQuery(id+"F0.wireOp",EDGE,"E48.1.0.15"),sQuery(id+"F0.wireOp",EDGE,"E48.1.0.16"),sQuery(id+"F0.wireOp",EDGE,"E48.1.0.17"),sQuery(id+"F0.wireOp",EDGE,"E48.1.0.18"),sQuery(id+"F0.wireOp",EDGE,"E48.1.0.19"),sQuery(id+"F0.wireOp",EDGE,"E48.1.0.20"),sQuery(id+"F0.wireOp",EDGE,"E48.1.0.21"),sQuery(id+"F0.wireOp",EDGE,"E48.2.0.0"),sQuery(id+"F0.wireOp",EDGE,"E48.2.0.2"),sQuery(id+"F0.wireOp",EDGE,"E48.2.0.3"),sQuery(id+"F0.wireOp",EDGE,"E48.2.0.5"),sQuery(id+"F0.wireOp",EDGE,"E48.2.0.6"),sQuery(id+"F0.wireOp",EDGE,"E48.2.0.7"),sQuery(id+"F0.wireOp",EDGE,"E48.2.0.8"),sQuery(id+"F0.wireOp",EDGE,"E48.2.0.9"),sQuery(id+"F0.wireOp",EDGE,"E48.2.0.12"),sQuery(id+"F0.wireOp",EDGE,"E48.2.0.13"),sQuery(id+"F0.wireOp",EDGE,"E48.2.0.14"),sQuery(id+"F0.wireOp",EDGE,"E48.2.0.15"),sQuery(id+"F0.wireOp",EDGE,"E48.2.0.16"),sQuery(id+"F0.wireOp",EDGE,"E48.2.0.17"),sQuery(id+"F0.wireOp",EDGE,"E48.2.0.18"),sQuery(id+"F0.wireOp",EDGE,"E48.2.0.19"),sQuery(id+"F0.wireOp",EDGE,"E48.2.0.20"),sQuery(id+"F0.wireOp",EDGE,"E48.2.0.21"),sQuery(id+"F0.wireOp",EDGE,"E49.1.0.0"),sQuery(id+"F0.wireOp",EDGE,"E49.1.0.1"),sQuery(id+"F0.wireOp",EDGE,"E49.1.0.2"),sQuery(id+"F0.wireOp",EDGE,"E49.1.0.4"),sQuery(id+"F0.wireOp",EDGE,"E49.1.0.6"),sQuery(id+"F0.wireOp",EDGE,"E49.1.0.7"),sQuery(id+"F0.wireOp",EDGE,"E49.1.0.9"),sQuery(id+"F0.wireOp",EDGE,"E49.1.0.10"),sQuery(id+"F0.wireOp",EDGE,"E49.1.0.12"),sQuery(id+"F0.wireOp",EDGE,"E49.1.0.14"),sQuery(id+"F0.wireOp",EDGE,"E49.1.0.16"),sQuery(id+"F0.wireOp",EDGE,"E49.1.0.18"),sQuery(id+"F0.wireOp",EDGE,"E49.1.0.19"),sQuery(id+"F0.wireOp",EDGE,"E49.1.0.20"),sQuery(id+"F0.wireOp",EDGE,"E49.1.0.26"),sQuery(id+"F0.wireOp",EDGE,"E49.1.0.28"),sQuery(id+"F0.wireOp",EDGE,"E49.1.0.29"),sQuery(id+"F0.wireOp",EDGE,"E49.1.0.30"),sQuery(id+"F0.wireOp",EDGE,"E49.2.0.0"),sQuery(id+"F0.wireOp",EDGE,"E49.2.0.1"),sQuery(id+"F0.wireOp",EDGE,"E49.2.0.2"),sQuery(id+"F0.wireOp",EDGE,"E49.2.0.4"),sQuery(id+"F0.wireOp",EDGE,"E49.2.0.6"),sQuery(id+"F0.wireOp",EDGE,"E49.2.0.7"),sQuery(id+"F0.wireOp",EDGE,"E49.2.0.9"),sQuery(id+"F0.wireOp",EDGE,"E49.2.0.10"),sQuery(id+"F0.wireOp",EDGE,"E49.2.0.12"),sQuery(id+"F0.wireOp",EDGE,"E49.2.0.14"),sQuery(id+"F0.wireOp",EDGE,"E49.2.0.16"),sQuery(id+"F0.wireOp",EDGE,"E49.2.0.18"),sQuery(id+"F0.wireOp",EDGE,"E49.2.0.19"),sQuery(id+"F0.wireOp",EDGE,"E49.2.0.20"),sQuery(id+"F0.wireOp",EDGE,"E49.2.0.26"),sQuery(id+"F0.wireOp",EDGE,"E49.2.0.28"),sQuery(id+"F0.wireOp",EDGE,"E49.2.0.29"),sQuery(id+"F0.wireOp",EDGE,"E49.2.0.30")])],"isStart":false});
            extrude(context, id + "F2", {"entities" : qUnion([Q0]), "operationType" : NewBodyOperationType.ADD, "depth" : 5 * mm});
        }
        {
            var Q0;
            Q0=makeQuery(id+"F2.opExtrude","CAP_FACE",FACE,{"disambiguationData":[OSD([sQuery(id+"F0.wireOp",EDGE,"E0.bottom"),sQuery(id+"F0.wireOp",EDGE,"E0.top"),sQuery(id+"F0.wireOp",EDGE,"E0.left"),sQuery(id+"F0.wireOp",EDGE,"E0.right"),sQuery(id+"F0.wireOp",EDGE,"E5"),sQuery(id+"F0.wireOp",EDGE,"E6"),sQuery(id+"F0.wireOp",EDGE,"E7"),sQuery(id+"F0.wireOp",EDGE,"E10"),sQuery(id+"F0.wireOp",EDGE,"E11"),sQuery(id+"F0.wireOp",EDGE,"E12"),sQuery(id+"F0.wireOp",EDGE,"E13"),sQuery(id+"F0.wireOp",EDGE,"E14"),sQuery(id+"F0.wireOp",EDGE,"E15"),sQuery(id+"F0.wireOp",EDGE,"E16"),sQuery(id+"F0.wireOp",EDGE,"E17.bottom"),sQuery(id+"F0.wireOp",EDGE,"E17.top"),sQuery(id+"F0.wireOp",EDGE,"E17.left"),sQuery(id+"F0.wireOp",EDGE,"E17.right"),sQuery(id+"F0.wireOp",EDGE,"E18"),sQuery(id+"F0.wireOp",EDGE,"E19"),sQuery(id+"F0.wireOp",EDGE,"E21.bottom"),sQuery(id+"F0.wireOp",EDGE,"E21.top"),sQuery(id+"F0.wireOp",EDGE,"E21.left"),sQuery(id+"F0.wireOp",EDGE,"E21.right"),sQuery(id+"F0.wireOp",EDGE,"E23.bottom"),sQuery(id+"F0.wireOp",EDGE,"E23.top"),sQuery(id+"F0.wireOp",EDGE,"E24.left"),sQuery(id+"F0.wireOp",EDGE,"E24.right"),sQuery(id+"F0.wireOp",EDGE,"E25.left"),sQuery(id+"F0.wireOp",EDGE,"E25.right"),sQuery(id+"F0.wireOp",EDGE,"E26.trimOffspring"),sQuery(id+"F0.wireOp",EDGE,"E27.trimOffspring"),sQuery(id+"F0.wireOp",EDGE,"E28.trimOffspring"),sQuery(id+"F0.wireOp",EDGE,"E29.trimOffspring"),sQuery(id+"F0.wireOp",EDGE,"E30.trimOffspring"),sQuery(id+"F0.wireOp",EDGE,"E31.trimOffspring"),sQuery(id+"F0.wireOp",EDGE,"E32.trimOffspring"),sQuery(id+"F0.wireOp",EDGE,"E33.trimOffspring"),sQuery(id+"F0.wireOp",EDGE,"E22.bottom"),sQuery(id+"F0.wireOp",EDGE,"E22.top"),sQuery(id+"F0.wireOp",EDGE,"E22.left"),sQuery(id+"F0.wireOp",EDGE,"E22.right"),sQuery(id+"F0.wireOp",EDGE,"E35.bottom"),sQuery(id+"F0.wireOp",EDGE,"E35.top"),sQuery(id+"F0.wireOp",EDGE,"E36.left"),sQuery(id+"F0.wireOp",EDGE,"E36.right"),sQuery(id+"F0.wireOp",EDGE,"E37.left"),sQuery(id+"F0.wireOp",EDGE,"E37.right"),sQuery(id+"F0.wireOp",EDGE,"E38.trimOffspring"),sQuery(id+"F0.wireOp",EDGE,"E39.trimOffspring"),sQuery(id+"F0.wireOp",EDGE,"E40.trimOffspring"),sQuery(id+"F0.wireOp",EDGE,"E41.trimOffspring"),sQuery(id+"F0.wireOp",EDGE,"E42.trimOffspring"),sQuery(id+"F0.wireOp",EDGE,"E43.trimOffspring"),sQuery(id+"F0.wireOp",EDGE,"E44.trimOffspring"),sQuery(id+"F0.wireOp",EDGE,"E45.trimOffspring"),sQuery(id+"F0.wireOp",EDGE,"E46.bottom"),sQuery(id+"F0.wireOp",EDGE,"E46.top"),sQuery(id+"F0.wireOp",EDGE,"E46.left"),sQuery(id+"F0.wireOp",EDGE,"E46.right"),sQuery(id+"F0.wireOp",EDGE,"E47.bottom"),sQuery(id+"F0.wireOp",EDGE,"E47.top"),sQuery(id+"F0.wireOp",EDGE,"E47.left"),sQuery(id+"F0.wireOp",EDGE,"E47.right"),sQuery(id+"F0.wireOp",EDGE,"E48.1.0.0"),sQuery(id+"F0.wireOp",EDGE,"E48.1.0.2"),sQuery(id+"F0.wireOp",EDGE,"E48.1.0.3"),sQuery(id+"F0.wireOp",EDGE,"E48.1.0.5"),sQuery(id+"F0.wireOp",EDGE,"E48.1.0.6"),sQuery(id+"F0.wireOp",EDGE,"E48.1.0.7"),sQuery(id+"F0.wireOp",EDGE,"E48.1.0.8"),sQuery(id+"F0.wireOp",EDGE,"E48.1.0.9"),sQuery(id+"F0.wireOp",EDGE,"E48.1.0.12"),sQuery(id+"F0.wireOp",EDGE,"E48.1.0.13"),sQuery(id+"F0.wireOp",EDGE,"E48.1.0.14"),sQuery(id+"F0.wireOp",EDGE,"E48.1.0.15"),sQuery(id+"F0.wireOp",EDGE,"E48.1.0.16"),sQuery(id+"F0.wireOp",EDGE,"E48.1.0.17"),sQuery(id+"F0.wireOp",EDGE,"E48.1.0.18"),sQuery(id+"F0.wireOp",EDGE,"E48.1.0.19"),sQuery(id+"F0.wireOp",EDGE,"E48.1.0.20"),sQuery(id+"F0.wireOp",EDGE,"E48.1.0.21"),sQuery(id+"F0.wireOp",EDGE,"E48.2.0.0"),sQuery(id+"F0.wireOp",EDGE,"E48.2.0.2"),sQuery(id+"F0.wireOp",EDGE,"E48.2.0.3"),sQuery(id+"F0.wireOp",EDGE,"E48.2.0.5"),sQuery(id+"F0.wireOp",EDGE,"E48.2.0.6"),sQuery(id+"F0.wireOp",EDGE,"E48.2.0.7"),sQuery(id+"F0.wireOp",EDGE,"E48.2.0.8"),sQuery(id+"F0.wireOp",EDGE,"E48.2.0.9"),sQuery(id+"F0.wireOp",EDGE,"E48.2.0.12"),sQuery(id+"F0.wireOp",EDGE,"E48.2.0.13"),sQuery(id+"F0.wireOp",EDGE,"E48.2.0.14"),sQuery(id+"F0.wireOp",EDGE,"E48.2.0.15"),sQuery(id+"F0.wireOp",EDGE,"E48.2.0.16"),sQuery(id+"F0.wireOp",EDGE,"E48.2.0.17"),sQuery(id+"F0.wireOp",EDGE,"E48.2.0.18"),sQuery(id+"F0.wireOp",EDGE,"E48.2.0.19"),sQuery(id+"F0.wireOp",EDGE,"E48.2.0.20"),sQuery(id+"F0.wireOp",EDGE,"E48.2.0.21"),sQuery(id+"F0.wireOp",EDGE,"E49.1.0.0"),sQuery(id+"F0.wireOp",EDGE,"E49.1.0.1"),sQuery(id+"F0.wireOp",EDGE,"E49.1.0.2"),sQuery(id+"F0.wireOp",EDGE,"E49.1.0.4"),sQuery(id+"F0.wireOp",EDGE,"E49.1.0.6"),sQuery(id+"F0.wireOp",EDGE,"E49.1.0.7"),sQuery(id+"F0.wireOp",EDGE,"E49.1.0.9"),sQuery(id+"F0.wireOp",EDGE,"E49.1.0.10"),sQuery(id+"F0.wireOp",EDGE,"E49.1.0.12"),sQuery(id+"F0.wireOp",EDGE,"E49.1.0.14"),sQuery(id+"F0.wireOp",EDGE,"E49.1.0.16"),sQuery(id+"F0.wireOp",EDGE,"E49.1.0.18"),sQuery(id+"F0.wireOp",EDGE,"E49.1.0.19"),sQuery(id+"F0.wireOp",EDGE,"E49.1.0.20"),sQuery(id+"F0.wireOp",EDGE,"E49.1.0.26"),sQuery(id+"F0.wireOp",EDGE,"E49.1.0.28"),sQuery(id+"F0.wireOp",EDGE,"E49.1.0.29"),sQuery(id+"F0.wireOp",EDGE,"E49.1.0.30"),sQuery(id+"F0.wireOp",EDGE,"E49.2.0.0"),sQuery(id+"F0.wireOp",EDGE,"E49.2.0.1"),sQuery(id+"F0.wireOp",EDGE,"E49.2.0.2"),sQuery(id+"F0.wireOp",EDGE,"E49.2.0.4"),sQuery(id+"F0.wireOp",EDGE,"E49.2.0.6"),sQuery(id+"F0.wireOp",EDGE,"E49.2.0.7"),sQuery(id+"F0.wireOp",EDGE,"E49.2.0.9"),sQuery(id+"F0.wireOp",EDGE,"E49.2.0.10"),sQuery(id+"F0.wireOp",EDGE,"E49.2.0.12"),sQuery(id+"F0.wireOp",EDGE,"E49.2.0.14"),sQuery(id+"F0.wireOp",EDGE,"E49.2.0.16"),sQuery(id+"F0.wireOp",EDGE,"E49.2.0.18"),sQuery(id+"F0.wireOp",EDGE,"E49.2.0.19"),sQuery(id+"F0.wireOp",EDGE,"E49.2.0.20"),sQuery(id+"F0.wireOp",EDGE,"E49.2.0.26"),sQuery(id+"F0.wireOp",EDGE,"E49.2.0.28"),sQuery(id+"F0.wireOp",EDGE,"E49.2.0.29"),sQuery(id+"F0.wireOp",EDGE,"E49.2.0.30")])],"isStart":false});
            var sketch = newSketch(context, id + "F3", { "sketchPlane" : qUnion([Q0])});
            skPoint(sketch, "E53.0", {"position": v(-111.5, 3.96) * mm});
            skLineSegment(sketch, "E54.bottom", {"start": v(-102.5, -5.04) * mm, "end": v(-120.5, -5.04) * mm});
            skLineSegment(sketch, "E54.top", {"start": v(-102.5, 12.96) * mm, "end": v(-120.5, 12.96) * mm});
            skLineSegment(sketch, "E54.left", {"start": v(-102.5, -5.04) * mm, "end": v(-102.5, 12.96) * mm});
            skLineSegment(sketch, "E54.right", {"start": v(-120.5, -5.04) * mm, "end": v(-120.5, 12.96) * mm});
            skPoint(sketch, "E55.0", {"position": v(-111.5, -21.04) * mm});
            skLineSegment(sketch, "E56.bottom", {"start": v(-102.5, -30.04) * mm, "end": v(-120.5, -30.04) * mm});
            skLineSegment(sketch, "E56.top", {"start": v(-102.5, -12.04) * mm, "end": v(-120.5, -12.04) * mm});
            skLineSegment(sketch, "E56.left", {"start": v(-102.5, -30.04) * mm, "end": v(-102.5, -12.04) * mm});
            skLineSegment(sketch, "E56.right", {"start": v(-120.5, -30.04) * mm, "end": v(-120.5, -12.04) * mm});
            skPoint(sketch, "E57.0", {"position": v(-121.5, -21.04) * mm});
            skPoint(sketch, "E57.1", {"position": v(-121.5, 3.96) * mm});
            skLineSegment(sketch, "E58.bottom", {"start": v(-120.5, -1.04) * mm, "end": v(-122.5, -1.04) * mm});
            skLineSegment(sketch, "E58.top", {"start": v(-120.5, 8.96) * mm, "end": v(-122.5, 8.96) * mm});
            skLineSegment(sketch, "E58.left", {"start": v(-120.5, -1.04) * mm, "end": v(-120.5, 8.96) * mm});
            skLineSegment(sketch, "E58.right", {"start": v(-122.5, -1.04) * mm, "end": v(-122.5, 8.96) * mm});
            skPoint(sketch, "E59.0", {"position": v(-101.5, 3.96) * mm});
            skLineSegment(sketch, "E60.bottom", {"start": v(-102.5, -1.04) * mm, "end": v(-100.5, -1.04) * mm});
            skLineSegment(sketch, "E60.top", {"start": v(-102.5, 8.96) * mm, "end": v(-100.5, 8.96) * mm});
            skLineSegment(sketch, "E60.left", {"start": v(-102.5, -1.04) * mm, "end": v(-102.5, 8.96) * mm});
            skLineSegment(sketch, "E60.right", {"start": v(-100.5, -1.04) * mm, "end": v(-100.5, 8.96) * mm});
            skPoint(sketch, "E61.1.0.0", {"position": v(-75.5, 3.96) * mm});
            skPoint(sketch, "E61.1.0.1", {"position": v(-95.5, 3.96) * mm});
            skLineSegment(sketch, "E61.1.0.2", {"start": v(-76.5, -1.04) * mm, "end": v(-74.5, -1.04) * mm});
            skLineSegment(sketch, "E61.1.0.3", {"start": v(-76.5, 8.96) * mm, "end": v(-74.5, 8.96) * mm});
            skLineSegment(sketch, "E61.1.0.4", {"start": v(-94.5, -1.04) * mm, "end": v(-96.5, -1.04) * mm});
            skLineSegment(sketch, "E61.1.0.5", {"start": v(-76.5, 12.96) * mm, "end": v(-94.5, 12.96) * mm});
            skLineSegment(sketch, "E61.1.0.6", {"start": v(-76.5, -5.04) * mm, "end": v(-76.5, 12.96) * mm});
            skPoint(sketch, "E61.1.0.7", {"position": v(-85.5, 3.96) * mm});
            skLineSegment(sketch, "E61.1.0.8", {"start": v(-94.5, 8.96) * mm, "end": v(-96.5, 8.96) * mm});
            skLineSegment(sketch, "E61.1.0.9", {"start": v(-76.5, -5.04) * mm, "end": v(-94.5, -5.04) * mm});
            skLineSegment(sketch, "E61.1.0.10", {"start": v(-94.5, -5.04) * mm, "end": v(-94.5, 12.96) * mm});
            skLineSegment(sketch, "E61.1.0.11", {"start": v(-96.5, -1.04) * mm, "end": v(-96.5, 8.96) * mm});
            skLineSegment(sketch, "E61.1.0.12", {"start": v(-74.5, -1.04) * mm, "end": v(-74.5, 8.96) * mm});
            skPoint(sketch, "E61.1.0.13", {"position": v(-95.5, 3.96) * mm});
            skLineSegment(sketch, "E61.1.0.14", {"start": v(-76.5, -1.04) * mm, "end": v(-76.5, 8.96) * mm});
            skPoint(sketch, "E61.1.0.15", {"position": v(-75.5, 3.96) * mm});
            skLineSegment(sketch, "E61.1.0.16", {"start": v(-94.5, -1.04) * mm, "end": v(-94.5, 8.96) * mm});
            skPoint(sketch, "E61.1.0.17", {"position": v(-85.5, 3.96) * mm});
            skPoint(sketch, "E61.2.0.0", {"position": v(-49.5, 3.96) * mm});
            skPoint(sketch, "E61.2.0.1", {"position": v(-69.5, 3.96) * mm});
            skLineSegment(sketch, "E61.2.0.2", {"start": v(-50.5, -1.04) * mm, "end": v(-48.5, -1.04) * mm});
            skLineSegment(sketch, "E61.2.0.3", {"start": v(-50.5, 8.96) * mm, "end": v(-48.5, 8.96) * mm});
            skLineSegment(sketch, "E61.2.0.4", {"start": v(-68.5, -1.04) * mm, "end": v(-70.5, -1.04) * mm});
            skLineSegment(sketch, "E61.2.0.5", {"start": v(-50.5, 12.96) * mm, "end": v(-68.5, 12.96) * mm});
            skLineSegment(sketch, "E61.2.0.6", {"start": v(-50.5, -5.04) * mm, "end": v(-50.5, 12.96) * mm});
            skPoint(sketch, "E61.2.0.7", {"position": v(-59.5, 3.96) * mm});
            skLineSegment(sketch, "E61.2.0.8", {"start": v(-68.5, 8.96) * mm, "end": v(-70.5, 8.96) * mm});
            skLineSegment(sketch, "E61.2.0.9", {"start": v(-50.5, -5.04) * mm, "end": v(-68.5, -5.04) * mm});
            skLineSegment(sketch, "E61.2.0.10", {"start": v(-68.5, -5.04) * mm, "end": v(-68.5, 12.96) * mm});
            skLineSegment(sketch, "E61.2.0.11", {"start": v(-70.5, -1.04) * mm, "end": v(-70.5, 8.96) * mm});
            skLineSegment(sketch, "E61.2.0.12", {"start": v(-48.5, -1.04) * mm, "end": v(-48.5, 8.96) * mm});
            skPoint(sketch, "E61.2.0.13", {"position": v(-69.5, 3.96) * mm});
            skLineSegment(sketch, "E61.2.0.14", {"start": v(-50.5, -1.04) * mm, "end": v(-50.5, 8.96) * mm});
            skPoint(sketch, "E61.2.0.15", {"position": v(-49.5, 3.96) * mm});
            skLineSegment(sketch, "E61.2.0.16", {"start": v(-68.5, -1.04) * mm, "end": v(-68.5, 8.96) * mm});
            skPoint(sketch, "E61.2.0.17", {"position": v(-59.5, 3.96) * mm});
            skLineSegment(sketch, "E61.direction1", {"start": v(-120.5, -5.04) * mm, "end": v(-94.5, -5.04) * mm, "construction": true});
            skLineSegment(sketch, "E62.bottom", {"start": v(-120.5, -26.04) * mm, "end": v(-122.5, -26.04) * mm});
            skLineSegment(sketch, "E62.top", {"start": v(-120.5, -16.04) * mm, "end": v(-122.5, -16.04) * mm});
            skLineSegment(sketch, "E62.left", {"start": v(-120.5, -26.04) * mm, "end": v(-120.5, -16.04) * mm});
            skLineSegment(sketch, "E62.right", {"start": v(-122.5, -26.04) * mm, "end": v(-122.5, -16.04) * mm});
            skPoint(sketch, "E63.0", {"position": v(-101.5, -21.04) * mm});
            skLineSegment(sketch, "E64.bottom", {"start": v(-102.5, -16.04) * mm, "end": v(-100.5, -16.04) * mm});
            skLineSegment(sketch, "E64.top", {"start": v(-102.5, -26.04) * mm, "end": v(-100.5, -26.04) * mm});
            skLineSegment(sketch, "E64.left", {"start": v(-102.5, -16.04) * mm, "end": v(-102.5, -26.04) * mm});
            skLineSegment(sketch, "E64.right", {"start": v(-100.5, -16.04) * mm, "end": v(-100.5, -26.04) * mm});
            skPoint(sketch, "E65.1.0.0", {"position": v(-95.5, -21.04) * mm});
            skLineSegment(sketch, "E65.1.0.1", {"start": v(-74.5, -16.04) * mm, "end": v(-74.5, -26.04) * mm});
            skLineSegment(sketch, "E65.1.0.2", {"start": v(-76.5, -26.04) * mm, "end": v(-74.5, -26.04) * mm});
            skLineSegment(sketch, "E65.1.0.3", {"start": v(-76.5, -30.04) * mm, "end": v(-76.5, -12.04) * mm});
            skLineSegment(sketch, "E65.1.0.4", {"start": v(-94.5, -30.04) * mm, "end": v(-94.5, -12.04) * mm});
            skLineSegment(sketch, "E65.1.0.5", {"start": v(-94.5, -16.04) * mm, "end": v(-96.5, -16.04) * mm});
            skLineSegment(sketch, "E65.1.0.6", {"start": v(-94.5, -26.04) * mm, "end": v(-96.5, -26.04) * mm});
            skLineSegment(sketch, "E65.1.0.7", {"start": v(-76.5, -30.04) * mm, "end": v(-94.5, -30.04) * mm});
            skPoint(sketch, "E65.1.0.8", {"position": v(-75.5, -21.04) * mm});
            skLineSegment(sketch, "E65.1.0.9", {"start": v(-76.5, -12.04) * mm, "end": v(-94.5, -12.04) * mm});
            skLineSegment(sketch, "E65.1.0.10", {"start": v(-76.5, -16.04) * mm, "end": v(-74.5, -16.04) * mm});
            skPoint(sketch, "E65.1.0.11", {"position": v(-85.5, -21.04) * mm});
            skLineSegment(sketch, "E65.1.0.12", {"start": v(-96.5, -26.04) * mm, "end": v(-96.5, -16.04) * mm});
            skLineSegment(sketch, "E65.1.0.13", {"start": v(-76.5, -16.04) * mm, "end": v(-76.5, -26.04) * mm});
            skLineSegment(sketch, "E65.1.0.14", {"start": v(-94.5, -26.04) * mm, "end": v(-94.5, -16.04) * mm});
            skPoint(sketch, "E65.1.0.15", {"position": v(-85.5, -21.04) * mm});
            skPoint(sketch, "E65.1.0.16", {"position": v(-75.5, -21.04) * mm});
            skPoint(sketch, "E65.1.0.17", {"position": v(-95.5, -21.04) * mm});
            skPoint(sketch, "E65.2.0.0", {"position": v(-69.5, -21.04) * mm});
            skLineSegment(sketch, "E65.2.0.1", {"start": v(-48.5, -16.04) * mm, "end": v(-48.5, -26.04) * mm});
            skLineSegment(sketch, "E65.2.0.2", {"start": v(-50.5, -26.04) * mm, "end": v(-48.5, -26.04) * mm});
            skLineSegment(sketch, "E65.2.0.3", {"start": v(-50.5, -30.04) * mm, "end": v(-50.5, -12.04) * mm});
            skLineSegment(sketch, "E65.2.0.4", {"start": v(-68.5, -30.04) * mm, "end": v(-68.5, -12.04) * mm});
            skLineSegment(sketch, "E65.2.0.5", {"start": v(-68.5, -16.04) * mm, "end": v(-70.5, -16.04) * mm});
            skLineSegment(sketch, "E65.2.0.6", {"start": v(-68.5, -26.04) * mm, "end": v(-70.5, -26.04) * mm});
            skLineSegment(sketch, "E65.2.0.7", {"start": v(-50.5, -30.04) * mm, "end": v(-68.5, -30.04) * mm});
            skPoint(sketch, "E65.2.0.8", {"position": v(-49.5, -21.04) * mm});
            skLineSegment(sketch, "E65.2.0.9", {"start": v(-50.5, -12.04) * mm, "end": v(-68.5, -12.04) * mm});
            skLineSegment(sketch, "E65.2.0.10", {"start": v(-50.5, -16.04) * mm, "end": v(-48.5, -16.04) * mm});
            skPoint(sketch, "E65.2.0.11", {"position": v(-59.5, -21.04) * mm});
            skLineSegment(sketch, "E65.2.0.12", {"start": v(-70.5, -26.04) * mm, "end": v(-70.5, -16.04) * mm});
            skLineSegment(sketch, "E65.2.0.13", {"start": v(-50.5, -16.04) * mm, "end": v(-50.5, -26.04) * mm});
            skLineSegment(sketch, "E65.2.0.14", {"start": v(-68.5, -26.04) * mm, "end": v(-68.5, -16.04) * mm});
            skPoint(sketch, "E65.2.0.15", {"position": v(-59.5, -21.04) * mm});
            skPoint(sketch, "E65.2.0.16", {"position": v(-49.5, -21.04) * mm});
            skPoint(sketch, "E65.2.0.17", {"position": v(-69.5, -21.04) * mm});
            skLineSegment(sketch, "E65.direction1", {"start": v(-120.5, -30.04) * mm, "end": v(-94.5, -30.04) * mm, "construction": true});
            skPoint(sketch, "E66.0", {"position": v(-134.5, 3.96) * mm});
            skPoint(sketch, "E66.1", {"position": v(-134.5, -21.04) * mm});
            skLineSegment(sketch, "E67.bottom", {"start": v(-129.5, -1.04) * mm, "end": v(-139.5, -1.04) * mm});
            skLineSegment(sketch, "E67.top", {"start": v(-129.5, 8.96) * mm, "end": v(-139.5, 8.96) * mm});
            skLineSegment(sketch, "E67.left", {"start": v(-129.5, -1.04) * mm, "end": v(-129.5, 8.96) * mm});
            skLineSegment(sketch, "E67.right", {"start": v(-139.5, -1.04) * mm, "end": v(-139.5, 8.96) * mm});
            skLineSegment(sketch, "E68.bottom", {"start": v(-129.5, -26.04) * mm, "end": v(-139.5, -26.04) * mm});
            skLineSegment(sketch, "E68.top", {"start": v(-129.5, -16.04) * mm, "end": v(-139.5, -16.04) * mm});
            skLineSegment(sketch, "E68.left", {"start": v(-129.5, -26.04) * mm, "end": v(-129.5, -16.04) * mm});
            skLineSegment(sketch, "E68.right", {"start": v(-139.5, -26.04) * mm, "end": v(-139.5, -16.04) * mm});
            skSolve(sketch);
        }
        {
            var Q0;
            Q0=qSketchRegion(id+"F3",true);
            extrude(context, id + "F4", {"entities" : qUnion([Q0]), "operationType" : NewBodyOperationType.REMOVE, "oppositeDirection" : true, "depth" : 5 * mm});
        }
        {
            var Q0;
            Q0=qCreatedBy(makeId("Top.planeOp"),FACE);
            var sketch = newSketch(context, id + "F5", { "sketchPlane" : qUnion([Q0])});
            skLineSegment(sketch, "E69.bottom", {"start": v(-106.79, 77.03) * mm, "end": v(-126.79, 77.03) * mm});
            skLineSegment(sketch, "E69.top", {"start": v(-106.79, 97.03) * mm, "end": v(-126.79, 97.03) * mm});
            skLineSegment(sketch, "E69.left", {"start": v(-106.79, 77.03) * mm, "end": v(-106.79, 97.03) * mm});
            skLineSegment(sketch, "E69.right", {"start": v(-126.79, 77.03) * mm, "end": v(-126.79, 97.03) * mm});
            skPoint(sketch, "E69.middle", {"position": v(-116.79, 87.03) * mm});
            skLineSegment(sketch, "E70.bottom", {"start": v(-105.79, 82.03) * mm, "end": v(-107.79, 82.03) * mm});
            skLineSegment(sketch, "E70.top", {"start": v(-105.79, 92.03) * mm, "end": v(-107.79, 92.03) * mm});
            skLineSegment(sketch, "E70.left", {"start": v(-105.79, 82.03) * mm, "end": v(-105.79, 92.03) * mm});
            skLineSegment(sketch, "E70.right", {"start": v(-107.79, 82.03) * mm, "end": v(-107.79, 92.03) * mm});
            skPoint(sketch, "E70.middle", {"position": v(-106.79, 87.03) * mm});
            skLineSegment(sketch, "E71.bottom", {"start": v(-125.79, 82.03) * mm, "end": v(-127.79, 82.03) * mm});
            skLineSegment(sketch, "E71.top", {"start": v(-125.79, 92.03) * mm, "end": v(-127.79, 92.03) * mm});
            skLineSegment(sketch, "E71.left", {"start": v(-125.79, 82.03) * mm, "end": v(-125.79, 92.03) * mm});
            skLineSegment(sketch, "E71.right", {"start": v(-127.79, 82.03) * mm, "end": v(-127.79, 92.03) * mm});
            skPoint(sketch, "E71.middle", {"position": v(-126.79, 87.03) * mm});
            skLineSegment(sketch, "E72.bottom", {"start": v(-107.79, 78.03) * mm, "end": v(-125.79, 78.03) * mm});
            skLineSegment(sketch, "E72.top", {"start": v(-107.79, 96.03) * mm, "end": v(-125.79, 96.03) * mm});
            skLineSegment(sketch, "E72.left", {"start": v(-107.79, 78.03) * mm, "end": v(-107.79, 96.03) * mm});
            skLineSegment(sketch, "E72.right", {"start": v(-125.79, 78.03) * mm, "end": v(-125.79, 96.03) * mm});
            skLineSegment(sketch, "E73.bottom", {"start": v(-107.79, 86.53) * mm, "end": v(-125.79, 86.53) * mm});
            skLineSegment(sketch, "E73.top", {"start": v(-107.79, 87.53) * mm, "end": v(-125.79, 87.53) * mm});
            skLineSegment(sketch, "E73.left", {"start": v(-107.79, 86.53) * mm, "end": v(-107.79, 87.53) * mm});
            skLineSegment(sketch, "E73.right", {"start": v(-125.79, 86.53) * mm, "end": v(-125.79, 87.53) * mm});
            skLineSegment(sketch, "E74.bottom", {"start": v(-115.79, 85.78) * mm, "end": v(-117.79, 85.78) * mm, "construction": true});
            skLineSegment(sketch, "E74.top", {"start": v(-115.79, 88.28) * mm, "end": v(-117.79, 88.28) * mm, "construction": true});
            skLineSegment(sketch, "E74.left", {"start": v(-115.79, 85.78) * mm, "end": v(-115.79, 88.28) * mm, "construction": true});
            skLineSegment(sketch, "E74.right", {"start": v(-117.79, 85.78) * mm, "end": v(-117.79, 88.28) * mm, "construction": true});
            skLineSegment(sketch, "E75.bottom", {"start": v(-110.82, 38.4) * mm, "end": v(-132.62, 38.4) * mm});
            skLineSegment(sketch, "E75.top", {"start": v(-110.82, 60.2) * mm, "end": v(-132.62, 60.2) * mm});
            skLineSegment(sketch, "E75.left", {"start": v(-110.82, 38.4) * mm, "end": v(-110.82, 60.2) * mm});
            skLineSegment(sketch, "E75.right", {"start": v(-132.62, 38.4) * mm, "end": v(-132.62, 60.2) * mm});
            skPoint(sketch, "E75.middle", {"position": v(-121.72, 49.3) * mm});
            skLineSegment(sketch, "E76.bottom", {"start": v(-110.82, 44.4) * mm, "end": v(-112.62, 44.4) * mm});
            skLineSegment(sketch, "E76.top", {"start": v(-110.82, 54.2) * mm, "end": v(-112.62, 54.2) * mm});
            skLineSegment(sketch, "E76.left", {"start": v(-110.82, 44.4) * mm, "end": v(-110.82, 54.2) * mm});
            skLineSegment(sketch, "E76.right", {"start": v(-112.62, 44.4) * mm, "end": v(-112.62, 54.2) * mm});
            skPoint(sketch, "E76.middle", {"position": v(-111.72, 49.3) * mm});
            skLineSegment(sketch, "E77.bottom", {"start": v(-130.82, 44.4) * mm, "end": v(-132.62, 44.4) * mm});
            skLineSegment(sketch, "E77.top", {"start": v(-130.82, 54.2) * mm, "end": v(-132.62, 54.2) * mm});
            skLineSegment(sketch, "E77.left", {"start": v(-130.82, 44.4) * mm, "end": v(-130.82, 54.2) * mm});
            skLineSegment(sketch, "E77.right", {"start": v(-132.62, 44.4) * mm, "end": v(-132.62, 54.2) * mm});
            skPoint(sketch, "E77.middle", {"position": v(-131.72, 49.3) * mm});
            skLineSegment(sketch, "E78.bottom", {"start": v(-112.62, 40.2) * mm, "end": v(-130.82, 40.2) * mm});
            skLineSegment(sketch, "E78.top", {"start": v(-112.62, 58.4) * mm, "end": v(-130.82, 58.4) * mm});
            skLineSegment(sketch, "E78.left", {"start": v(-112.62, 40.2) * mm, "end": v(-112.62, 58.4) * mm});
            skLineSegment(sketch, "E78.right", {"start": v(-130.82, 40.2) * mm, "end": v(-130.82, 58.4) * mm});
            skSolve(sketch);
        }
        {
            var Q0;
            {var subQ11=sQuery(id+"F5.wireOp",EDGE,"E75.bottom");Q0=makeQuery(id+"F5.imprint","IMPRINT",FACE,{"disambiguationData":[TD([[makeQuery(id+"F5.imprint","IMPRINT",EDGE,{"derivedFrom":subQ11}),-1.0]])]});}
            var Q1;
            {var subQ5=sQuery(id+"F5.wireOp",EDGE,"E76.right");Q1=makeQuery(id+"F5.imprint","IMPRINT",FACE,{"disambiguationData":[TD([[makeQuery(id+"F5.imprint","IMPRINT",EDGE,{"derivedFrom":subQ5}),-1.0]])]});}
            var Q2;
            {var subQ5=sQuery(id+"F5.wireOp",EDGE,"E77.left");Q2=makeQuery(id+"F5.imprint","IMPRINT",FACE,{"disambiguationData":[TD([[makeQuery(id+"F5.imprint","IMPRINT",EDGE,{"derivedFrom":subQ5}),1.0]])]});}
            var Q3;
            {var subQ0=sQuery(id+"F5.wireOp",EDGE,"E77.bottom");Q3=makeQuery(id+"F5.imprint","IMPRINT",FACE,{"disambiguationData":[TD([[makeQuery(id+"F5.imprint","IMPRINT",EDGE,{"derivedFrom":subQ0}),-1.0]])]});}
            var Q4;
            {var subQ2=sQuery(id+"F5.wireOp",EDGE,"E75.top");Q4=makeQuery(id+"F5.imprint","IMPRINT",FACE,{"disambiguationData":[TD([[makeQuery(id+"F5.imprint","IMPRINT",EDGE,{"derivedFrom":subQ2}),1.0]])]});}
            var Q5;
            {var subQ0=sQuery(id+"F5.wireOp",EDGE,"E76.bottom");Q5=makeQuery(id+"F5.imprint","IMPRINT",FACE,{"disambiguationData":[TD([[makeQuery(id+"F5.imprint","IMPRINT",EDGE,{"derivedFrom":subQ0}),-1.0]])]});}
            extrude(context, id + "F6", {"entities" : qUnion([Q0, Q1, Q2, Q3, Q4, Q5]), "depth" : 1 * mm});
        }
        {
            var Q0;
            {var subQ5=sQuery(id+"F5.wireOp",EDGE,"E77.right");Q0=makeQuery(id+"F5.imprint","IMPRINT",FACE,{"disambiguationData":[TD([[makeQuery(id+"F5.imprint","IMPRINT",EDGE,{"derivedFrom":subQ5}),-1.0]])]});}
            var Q1;
            {var subQ5=sQuery(id+"F5.wireOp",EDGE,"E77.left");Q1=makeQuery(id+"F5.imprint","IMPRINT",FACE,{"disambiguationData":[TD([[makeQuery(id+"F5.imprint","IMPRINT",EDGE,{"derivedFrom":subQ5}),1.0]])]});}
            var Q2;
            {var subQ5=sQuery(id+"F5.wireOp",EDGE,"E76.right");Q2=makeQuery(id+"F5.imprint","IMPRINT",FACE,{"disambiguationData":[TD([[makeQuery(id+"F5.imprint","IMPRINT",EDGE,{"derivedFrom":subQ5}),-1.0]])]});}
            var Q3;
            {var subQ5=sQuery(id+"F5.wireOp",EDGE,"E76.left");Q3=makeQuery(id+"F5.imprint","IMPRINT",FACE,{"disambiguationData":[TD([[makeQuery(id+"F5.imprint","IMPRINT",EDGE,{"derivedFrom":subQ5}),1.0]])]});}
            extrude(context, id + "F7", {"entities" : qUnion([Q0, Q1, Q2, Q3]), "operationType" : NewBodyOperationType.ADD, "oppositeDirection" : true, "depth" : 4 * mm});
        }
        {
            var Q0;
            Q0=makeQuery(id+"F6.opExtrude","CAP_FACE",FACE,{"disambiguationData":[OSD([sQuery(id+"F5.wireOp",EDGE,"E75.bottom"),sQuery(id+"F5.wireOp",EDGE,"E75.top"),sQuery(id+"F5.wireOp",EDGE,"E75.left"),sQuery(id+"F5.wireOp",EDGE,"E75.right"),sQuery(id+"F5.wireOp",EDGE,"E76.left"),sQuery(id+"F5.wireOp",EDGE,"E77.right"),sQuery(id+"F5.wireOp",EDGE,"E78.bottom"),sQuery(id+"F5.wireOp",EDGE,"E78.top"),sQuery(id+"F5.wireOp",EDGE,"E78.left"),sQuery(id+"F5.wireOp",EDGE,"E78.right")])],"isStart":false});
            var sketch = newSketch(context, id + "F8", { "sketchPlane" : qUnion([Q0])});
            skPoint(sketch, "E79.0", {"position": v(-121.72, 49.3) * mm});
            skLineSegment(sketch, "E80.bottom", {"start": v(-112.62, 40.2) * mm, "end": v(-130.82, 40.2) * mm});
            skLineSegment(sketch, "E80.top", {"start": v(-112.62, 58.4) * mm, "end": v(-130.82, 58.4) * mm});
            skLineSegment(sketch, "E80.left", {"start": v(-112.62, 40.2) * mm, "end": v(-112.62, 58.4) * mm});
            skLineSegment(sketch, "E80.right", {"start": v(-130.82, 40.2) * mm, "end": v(-130.82, 58.4) * mm});
            skLineSegment(sketch, "E81.0", {"start": v(-131.82, 39.2) * mm, "end": v(-131.82, 59.4) * mm});
            skLineSegment(sketch, "E81.1", {"start": v(-111.62, 39.2) * mm, "end": v(-131.82, 39.2) * mm});
            skLineSegment(sketch, "E81.2", {"start": v(-111.62, 39.2) * mm, "end": v(-111.62, 59.4) * mm});
            skLineSegment(sketch, "E81.3", {"start": v(-111.62, 59.4) * mm, "end": v(-131.82, 59.4) * mm});
            skSolve(sketch);
        }
        {
            var Q0;
            Q0=makeQuery(id+"F8.imprint","IMPRINT",FACE,{"disambiguationData":[TD([[makeQuery(id+"F8.imprint","IMPRINT",EDGE,{"derivedFrom":sQuery(id+"F8.wireOp",EDGE,"E80.bottom")}),1.0]])]});
            extrude(context, id + "F9", {"entities" : qUnion([Q0]), "operationType" : NewBodyOperationType.ADD, "depth" : 5 * mm});
        }
        {
            var Q0;
            Q0=makeQuery(id+"F9.opExtrude","CAP_FACE",FACE,{"disambiguationData":[OSD([sQuery(id+"F8.wireOp",EDGE,"E80.bottom"),sQuery(id+"F8.wireOp",EDGE,"E80.top"),sQuery(id+"F8.wireOp",EDGE,"E80.left"),sQuery(id+"F8.wireOp",EDGE,"E80.right"),sQuery(id+"F8.wireOp",EDGE,"E81.0"),sQuery(id+"F8.wireOp",EDGE,"E81.1"),sQuery(id+"F8.wireOp",EDGE,"E81.2"),sQuery(id+"F8.wireOp",EDGE,"E81.3")])],"isStart":false});
            var sketch = newSketch(context, id + "F10", { "sketchPlane" : qUnion([Q0])});
            skPoint(sketch, "E82.0", {"position": v(-121.72, 49.3) * mm});
            skLineSegment(sketch, "E83.bottom", {"start": v(-112.62, 48.8) * mm, "end": v(-130.82, 48.8) * mm});
            skLineSegment(sketch, "E83.top", {"start": v(-112.62, 49.8) * mm, "end": v(-130.82, 49.8) * mm});
            skLineSegment(sketch, "E83.left", {"start": v(-112.62, 48.8) * mm, "end": v(-112.62, 49.8) * mm});
            skLineSegment(sketch, "E83.right", {"start": v(-130.82, 48.8) * mm, "end": v(-130.82, 49.8) * mm});
            skLineSegment(sketch, "E84.bottom", {"start": v(-121.22, 40.2) * mm, "end": v(-122.22, 40.2) * mm});
            skLineSegment(sketch, "E84.top", {"start": v(-121.22, 58.4) * mm, "end": v(-122.22, 58.4) * mm});
            skLineSegment(sketch, "E84.left", {"start": v(-121.22, 40.2) * mm, "end": v(-121.22, 58.4) * mm});
            skLineSegment(sketch, "E84.right", {"start": v(-122.22, 40.2) * mm, "end": v(-122.22, 58.4) * mm});
            skSolve(sketch);
        }
        {
            var Q0;
            Q0=makeQuery(id+"FvrxBWBR3NFs59h_1.boolean.opBoolean","MERGE",FACE,{"derivedFrom":[makeQuery(id+"F4.boolean.opBoolean","COPY",FACE,{"derivedFrom":makeQuery(id+"F4.opExtrude","CAP_FACE",FACE,{"disambiguationData":[OSD([sQuery(id+"F3.wireOp",EDGE,"E54.bottom"),sQuery(id+"F3.wireOp",EDGE,"E54.top"),sQuery(id+"F3.wireOp",EDGE,"E54.left"),sQuery(id+"F3.wireOp",EDGE,"E54.right")])],"isStart":false})}),makeQuery(id+"FvrxBWBR3NFs59h_1.opExtrude","CAP_FACE",FACE,{"disambiguationData":[OSD([sQuery(id+"FOyiDT4y5zkIJA3_1.wireOp",EDGE,"oN5qgFBu-MPa5-jxRP-8K83-Y7W6XuHjnRPn.bottom"),sQuery(id+"FOyiDT4y5zkIJA3_1.wireOp",EDGE,"oN5qgFBu-MPa5-jxRP-8K83-Y7W6XuHjnRPn.top"),sQuery(id+"FOyiDT4y5zkIJA3_1.wireOp",EDGE,"oN5qgFBu-MPa5-jxRP-8K83-Y7W6XuHjnRPn.left"),sQuery(id+"FOyiDT4y5zkIJA3_1.wireOp",EDGE,"oN5qgFBu-MPa5-jxRP-8K83-Y7W6XuHjnRPn.right")])],"isStart":false}),makeQuery(id+"FvrxBWBR3NFs59h_1.opExtrude","CAP_FACE",FACE,{"disambiguationData":[OSD([sQuery(id+"FOyiDT4y5zkIJA3_1.wireOp",EDGE,"if443p5T-YKs4-1gVt-ORIe-qeo7ftMrQxsQ.bottom"),sQuery(id+"FOyiDT4y5zkIJA3_1.wireOp",EDGE,"if443p5T-YKs4-1gVt-ORIe-qeo7ftMrQxsQ.top"),sQuery(id+"FOyiDT4y5zkIJA3_1.wireOp",EDGE,"if443p5T-YKs4-1gVt-ORIe-qeo7ftMrQxsQ.left"),sQuery(id+"FOyiDT4y5zkIJA3_1.wireOp",EDGE,"if443p5T-YKs4-1gVt-ORIe-qeo7ftMrQxsQ.right")])],"isStart":false})]});
            var sketch = newSketch(context, id + "F11", { "sketchPlane" : qUnion([Q0])});
            skPoint(sketch, "E85.0", {"position": v(-111.5, 3.96) * mm});
            skLineSegment(sketch, "E86.bottom", {"start": v(-108.5, 0.96) * mm, "end": v(-114.5, 0.96) * mm});
            skLineSegment(sketch, "E86.top", {"start": v(-108.5, 6.96) * mm, "end": v(-114.5, 6.96) * mm});
            skLineSegment(sketch, "E86.left", {"start": v(-108.5, 0.96) * mm, "end": v(-108.5, 6.96) * mm});
            skLineSegment(sketch, "E86.right", {"start": v(-114.5, 0.96) * mm, "end": v(-114.5, 6.96) * mm});
            skSolve(sketch);
        }
        {
            var Q0;
            {var subQ0=sQuery(id+"F11.wireOp",EDGE,"E86.top");Q0=makeQuery(id+"F11.imprint","IMPRINT",FACE,{"disambiguationData":[TD([[makeQuery(id+"F11.imprint","IMPRINT",EDGE,{"derivedFrom":subQ0}),1.0]])]});}
            var Q1;
            {var subQ0=sQuery(id+"F11.wireOp",EDGE,"E86.left");var subQ1=makeQuery(id+"F4.opExtrude","CAP_FACE",FACE,{"disambiguationData":[OSD([sQuery(id+"F3.wireOp",EDGE,"E54.bottom"),sQuery(id+"F3.wireOp",EDGE,"E54.top"),sQuery(id+"F3.wireOp",EDGE,"E54.left"),sQuery(id+"F3.wireOp",EDGE,"E54.right")])],"isStart":false});var subQ2=sQuery(id+"F0.wireOp",EDGE,"E33.trimOffspring");var subQ3=makeQuery(id+"F4.boolean.opBoolean","INTERSECT",EDGE,{"derivedFrom":[makeQuery(id+"F2.boolean.opBoolean","MERGE",FACE,{"derivedFrom":[makeQuery(id+"F1.opExtrude","SWEPT_FACE",FACE,{"disambiguationData":[OSD([subQ2])]}),makeQuery(id+"F2.opExtrude","SWEPT_FACE",FACE,{"disambiguationData":[OSD([subQ2])]})]}),subQ1]});var subQ4=makeQuery(id+"F11.imprint","INTERSECT",VERTEX,{"derivedFrom":[subQ3,subQ0]});Q1=makeQuery(id+"F11.imprint","IMPRINT",FACE,{"disambiguationData":[TD([[makeQuery(id+"F11.imprint","IMPRINT",EDGE,{"disambiguationData":[TD([[subQ4,-1.0]])],"derivedFrom":subQ0}),1.0]])]});}
            var Q2;
            {var subQ0=sQuery(id+"F11.wireOp",EDGE,"E86.bottom");Q2=makeQuery(id+"F11.imprint","IMPRINT",FACE,{"disambiguationData":[TD([[makeQuery(id+"F11.imprint","IMPRINT",EDGE,{"derivedFrom":subQ0}),-1.0]])]});}
            extrude(context, id + "F12", {"entities" : qUnion([Q0, Q1, Q2]), "operationType" : NewBodyOperationType.ADD, "depth" : 8 * mm});
        }
        {
            var Q0;
            Q0=qSketchRegion(id+"F10",true);
            extrude(context, id + "F13", {"entities" : qUnion([Q0]), "operationType" : NewBodyOperationType.ADD, "oppositeDirection" : true, "depth" : 6 * mm});
        }
        {
            var Q0;
            Q0=makeQuery(id+"F13.boolean.opBoolean","MERGE",FACE,{"derivedFrom":[makeQuery(id+"F9.opExtrude","CAP_FACE",FACE,{"disambiguationData":[OSD([sQuery(id+"F8.wireOp",EDGE,"E80.bottom"),sQuery(id+"F8.wireOp",EDGE,"E80.top"),sQuery(id+"F8.wireOp",EDGE,"E80.left"),sQuery(id+"F8.wireOp",EDGE,"E80.right"),sQuery(id+"F8.wireOp",EDGE,"E81.0"),sQuery(id+"F8.wireOp",EDGE,"E81.1"),sQuery(id+"F8.wireOp",EDGE,"E81.2"),sQuery(id+"F8.wireOp",EDGE,"E81.3")])],"isStart":false}),makeQuery(id+"F13.opExtrude","CAP_FACE",FACE,{"disambiguationData":[OSD([sQuery(id+"F10.wireOp",EDGE,"E83.bottom"),sQuery(id+"F10.wireOp",EDGE,"E83.top"),sQuery(id+"F10.wireOp",EDGE,"E83.left"),sQuery(id+"F10.wireOp",EDGE,"E83.right"),sQuery(id+"F10.wireOp",EDGE,"E84.bottom"),sQuery(id+"F10.wireOp",EDGE,"E84.top"),sQuery(id+"F10.wireOp",EDGE,"E84.left"),sQuery(id+"F10.wireOp",EDGE,"E84.right")])],"isStart":true})]});
            var sketch = newSketch(context, id + "F14", { "sketchPlane" : qUnion([Q0])});
            skPoint(sketch, "E87.0", {"position": v(-130.82, 58.4) * mm});
            skPoint(sketch, "E87.1", {"position": v(-112.62, 40.2) * mm});
            skLineSegment(sketch, "E88.bottom", {"start": v(-130.82, 58.4) * mm, "end": v(-112.62, 58.4) * mm});
            skLineSegment(sketch, "E88.top", {"start": v(-130.82, 40.2) * mm, "end": v(-112.62, 40.2) * mm});
            skLineSegment(sketch, "E88.left", {"start": v(-130.82, 58.4) * mm, "end": v(-130.82, 40.2) * mm});
            skLineSegment(sketch, "E88.right", {"start": v(-112.62, 58.4) * mm, "end": v(-112.62, 40.2) * mm});
            skSolve(sketch);
        }
        {
            var Q0;
            Q0=qSketchRegion(id+"F14",true);
            extrude(context, id + "F15", {"entities" : qUnion([Q0]), "operationType" : NewBodyOperationType.REMOVE, "oppositeDirection" : true, "depth" : 1 * mm});
        }
        {
            var Q0;
            {var subQ0=sQuery(id+"F5.wireOp",EDGE,"E77.right");var subQ2=sQuery(id+"F5.wireOp",EDGE,"E78.right");var subQ4=sQuery(id+"F5.wireOp",EDGE,"E76.left");var subQ6=sQuery(id+"F5.wireOp",EDGE,"E78.left");var subQ8=sQuery(id+"F5.wireOp",EDGE,"E75.top");var subQ9=sQuery(id+"F5.wireOp",EDGE,"E75.left");var subQ11=sQuery(id+"F5.wireOp",EDGE,"E75.right");var subQ13=sQuery(id+"F5.wireOp",EDGE,"E78.top");var subQ16=sQuery(id+"F5.wireOp",EDGE,"E78.bottom");var subQ17=sQuery(id+"F5.wireOp",EDGE,"E75.bottom");var subQ18=makeQuery(id+"F6.opExtrude","CAP_FACE",FACE,{"disambiguationData":[OSD([subQ17,subQ8,subQ9,subQ11,subQ4,subQ0,subQ16,subQ13,subQ6,subQ2])],"isStart":true});Q0=makeQuery(id+"F13.boolean.opBoolean","MERGE",FACE,{"derivedFrom":[makeQuery(id+"F7.boolean.opBoolean","SPLIT",FACE,{"disambiguationData":[TD([makeQuery(id+"F6.opExtrude","SWEPT_FACE",FACE,{"disambiguationData":[OSD([subQ17])]})])],"derivedFrom":subQ18}),makeQuery(id+"F7.boolean.opBoolean","SPLIT",FACE,{"disambiguationData":[TD([makeQuery(id+"F6.opExtrude","SWEPT_FACE",FACE,{"disambiguationData":[OSD([subQ8])]})])],"derivedFrom":subQ18}),makeQuery(id+"F13.opExtrude","CAP_FACE",FACE,{"disambiguationData":[OSD([sQuery(id+"F10.wireOp",EDGE,"E83.bottom"),sQuery(id+"F10.wireOp",EDGE,"E83.top"),sQuery(id+"F10.wireOp",EDGE,"E83.left"),sQuery(id+"F10.wireOp",EDGE,"E83.right"),sQuery(id+"F10.wireOp",EDGE,"E84.bottom"),sQuery(id+"F10.wireOp",EDGE,"E84.top"),sQuery(id+"F10.wireOp",EDGE,"E84.left"),sQuery(id+"F10.wireOp",EDGE,"E84.right")])],"isStart":false})]});}
            var sketch = newSketch(context, id + "F16", { "sketchPlane" : qUnion([Q0])});
            skPoint(sketch, "E89.0", {"position": v(-121.72, -40.2) * mm});
            skLineSegment(sketch, "E90.bottom", {"start": v(-120.72, -50.54) * mm, "end": v(-122.72, -50.54) * mm});
            skLineSegment(sketch, "E90.top", {"start": v(-120.72, -48.04) * mm, "end": v(-122.72, -48.04) * mm});
            skLineSegment(sketch, "E90.left", {"start": v(-120.72, -50.54) * mm, "end": v(-120.72, -48.04) * mm});
            skLineSegment(sketch, "E90.right", {"start": v(-122.72, -50.54) * mm, "end": v(-122.72, -48.04) * mm});
            skPoint(sketch, "E90.middle", {"position": v(-121.72, -49.3) * mm});
            skPoint(sketch, "E90.middle.positionSnap0", {"position": v(-130.82, -49.3) * mm});
            skPoint(sketch, "E90.centerSnap0", {"position": v(-130.82, -49.3) * mm});
            skSolve(sketch);
        }
        {
            var Q0;
            Q0=makeQuery(id+"F12.opExtrude","CAP_FACE",FACE,{"disambiguationData":[OSD([sQuery(id+"F11.wireOp",EDGE,"E86.bottom"),sQuery(id+"F11.wireOp",EDGE,"E86.top"),sQuery(id+"F11.wireOp",EDGE,"E86.left"),sQuery(id+"F11.wireOp",EDGE,"E86.right")])],"isStart":false});
            var sketch = newSketch(context, id + "F17", { "sketchPlane" : qUnion([Q0])});
            skPoint(sketch, "E91.0", {"position": v(-111.5, 3.96) * mm});
            skLineSegment(sketch, "E92.bottom", {"start": v(-110.5, 2.7) * mm, "end": v(-112.5, 2.7) * mm});
            skLineSegment(sketch, "E92.top", {"start": v(-110.5, 5.2) * mm, "end": v(-112.5, 5.2) * mm});
            skLineSegment(sketch, "E92.left", {"start": v(-110.5, 2.7) * mm, "end": v(-110.5, 5.2) * mm});
            skLineSegment(sketch, "E92.right", {"start": v(-112.5, 2.7) * mm, "end": v(-112.5, 5.2) * mm});
            skSolve(sketch);
        }
        {
            var Q0;
            Q0=qSketchRegion(id+"F17",true);
            extrude(context, id + "F18", {"entities" : qUnion([Q0]), "operationType" : NewBodyOperationType.ADD, "depth" : 2 * mm});
        }
        {
            var Q0;
            {var subQ0=sQuery(id+"F10.wireOp",EDGE,"E83.right");var subQ1=sQuery(id+"F10.wireOp",EDGE,"E83.bottom");var subQ4=sQuery(id+"F10.wireOp",EDGE,"E84.right");var subQ5=sQuery(id+"F5.wireOp",EDGE,"E78.right");var subQ8=sQuery(id+"F10.wireOp",EDGE,"E83.top");var subQ9=sQuery(id+"F5.wireOp",EDGE,"E77.right");var subQ11=sQuery(id+"F5.wireOp",EDGE,"E76.left");var subQ13=sQuery(id+"F5.wireOp",EDGE,"E78.left");var subQ15=sQuery(id+"F5.wireOp",EDGE,"E75.top");var subQ16=sQuery(id+"F5.wireOp",EDGE,"E75.left");var subQ18=sQuery(id+"F5.wireOp",EDGE,"E75.right");var subQ20=sQuery(id+"F5.wireOp",EDGE,"E78.top");var subQ22=sQuery(id+"F5.wireOp",EDGE,"E78.bottom");var subQ23=sQuery(id+"F5.wireOp",EDGE,"E75.bottom");var subQ24=makeQuery(id+"F6.opExtrude","CAP_FACE",FACE,{"disambiguationData":[OSD([subQ23,subQ15,subQ16,subQ18,subQ11,subQ9,subQ22,subQ20,subQ13,subQ5])],"isStart":true});Q0=makeQuery(id+"F21.boolean.opBoolean","SPLIT",FACE,{"disambiguationData":[TD([makeQuery(id+"F21.opExtrude","SWEPT_FACE",FACE,{"disambiguationData":[OSD([sQuery(id+"F16.wireOp",EDGE,"E90.right")])]})])],"derivedFrom":makeQuery(id+"F13.boolean.opBoolean","MERGE",FACE,{"derivedFrom":[makeQuery(id+"F7.boolean.opBoolean","SPLIT",FACE,{"disambiguationData":[TD([makeQuery(id+"F6.opExtrude","SWEPT_FACE",FACE,{"disambiguationData":[OSD([subQ23])]})])],"derivedFrom":subQ24}),makeQuery(id+"F7.boolean.opBoolean","SPLIT",FACE,{"disambiguationData":[TD([makeQuery(id+"F6.opExtrude","SWEPT_FACE",FACE,{"disambiguationData":[OSD([subQ15])]})])],"derivedFrom":subQ24}),makeQuery(id+"F13.opExtrude","CAP_FACE",FACE,{"disambiguationData":[OSD([subQ1,subQ8,sQuery(id+"F10.wireOp",EDGE,"E83.left"),subQ0,sQuery(id+"F10.wireOp",EDGE,"E84.bottom"),sQuery(id+"F10.wireOp",EDGE,"E84.top"),sQuery(id+"F10.wireOp",EDGE,"E84.left"),subQ4])],"isStart":false})]})});}
            var sketch = newSketch(context, id + "F19", { "sketchPlane" : qUnion([Q0])});
            skPoint(sketch, "E93.0", {"position": v(-126.52, -48.8) * mm});
            skPoint(sketch, "E94.0", {"position": v(-122.22, -44.5) * mm});
            skPoint(sketch, "E95.0", {"position": v(-122.22, -40.2) * mm});
            skLineSegment(sketch, "E96.bottom", {"start": v(-122.22, -40.2) * mm, "end": v(-130.82, -40.2) * mm});
            skLineSegment(sketch, "E96.top", {"start": v(-122.22, -48.8) * mm, "end": v(-130.82, -48.8) * mm});
            skLineSegment(sketch, "E96.left", {"start": v(-122.22, -40.2) * mm, "end": v(-122.22, -48.8) * mm});
            skLineSegment(sketch, "E96.right", {"start": v(-130.82, -40.2) * mm, "end": v(-130.82, -48.8) * mm});
            skPoint(sketch, "E96.middle", {"position": v(-126.52, -44.5) * mm});
            skLineSegment(sketch, "E97.bottom", {"start": v(-122.72, -40.7) * mm, "end": v(-130.32, -40.7) * mm});
            skLineSegment(sketch, "E97.top", {"start": v(-122.72, -48.3) * mm, "end": v(-130.32, -48.3) * mm});
            skLineSegment(sketch, "E97.left", {"start": v(-122.72, -40.7) * mm, "end": v(-122.72, -48.3) * mm});
            skLineSegment(sketch, "E97.right", {"start": v(-130.32, -40.7) * mm, "end": v(-130.32, -48.3) * mm});
            skLineSegment(sketch, "E98.direction1", {"start": v(-130.82, -48.8) * mm, "end": v(-121.22, -48.8) * mm, "construction": true});
            skLineSegment(sketch, "E99.0.1.0", {"start": v(-113.12, -40.7) * mm, "end": v(-120.72, -40.7) * mm});
            skLineSegment(sketch, "E99.3.1.0", {"start": v(-112.62, -40.2) * mm, "end": v(-121.22, -40.2) * mm});
            skLineSegment(sketch, "E99.6.1.0", {"start": v(-112.62, -48.8) * mm, "end": v(-121.22, -48.8) * mm});
            skLineSegment(sketch, "E99.9.1.0", {"start": v(-112.62, -40.2) * mm, "end": v(-112.62, -48.8) * mm});
            skPoint(sketch, "E99.12.1.0", {"position": v(-116.92, -44.5) * mm});
            skLineSegment(sketch, "E99.13.1.0", {"start": v(-113.12, -40.7) * mm, "end": v(-113.12, -48.3) * mm});
            skLineSegment(sketch, "E99.16.1.0", {"start": v(-120.72, -40.7) * mm, "end": v(-120.72, -48.3) * mm});
            skLineSegment(sketch, "E99.19.1.0", {"start": v(-121.22, -40.2) * mm, "end": v(-121.22, -48.8) * mm});
            skPoint(sketch, "E99.22.1.0", {"position": v(-112.62, -44.5) * mm});
            skPoint(sketch, "E99.23.1.0", {"position": v(-112.62, -40.2) * mm});
            skLineSegment(sketch, "E99.24.1.0", {"start": v(-113.12, -48.3) * mm, "end": v(-120.72, -48.3) * mm});
            skPoint(sketch, "E99.27.1.0", {"position": v(-116.92, -48.8) * mm});
            skPoint(sketch, "E99.28.1.0", {"position": v(-116.92, -44.5) * mm});
            skSolve(sketch);
        }
        {
            var Q0;
            Q0=qSketchRegion(id+"F19",true);
            extrude(context, id + "F20", {"entities" : qUnion([Q0]), "operationType" : NewBodyOperationType.ADD, "oppositeDirection" : true, "depth" : 2 * mm});
        }
        {
            var Q0;
            Q0=qSketchRegion(id+"F16",true);
            extrude(context, id + "F21", {"entities" : qUnion([Q0]), "operationType" : NewBodyOperationType.REMOVE, "oppositeDirection" : true, "depth" : 2 * mm});
        }
        {
            var Q0;
            Q0=makeQuery(id+"F0.imprint","IMPRINT",FACE,{"disambiguationData":[TD([[makeQuery(id+"F0.imprint","IMPRINT",EDGE,{"derivedFrom":sQuery(id+"F0.wireOp",EDGE,"E0.bottom")}),-1.0]])]});
            var sketch = newSketch(context, id + "F22", { "sketchPlane" : qUnion([Q0])});
            skPoint(sketch, "E100.0", {"position": v(-155, -55.04) * mm});
            skPoint(sketch, "E100.1", {"position": v(-10, -55.04) * mm});
            skPoint(sketch, "E100.2", {"position": v(-10, 19.96) * mm});
            skLineSegment(sketch, "E101.bottom", {"start": v(-155, -55.04) * mm, "end": v(-10, -55.04) * mm});
            skLineSegment(sketch, "E101.top", {"start": v(-155, -34.04) * mm, "end": v(-46, -34.04) * mm});
            skLineSegment(sketch, "E101.left", {"start": v(-155, -55.04) * mm, "end": v(-155, -34.04) * mm});
            skLineSegment(sketch, "E101.right", {"start": v(-10, -55.04) * mm, "end": v(-10, -34.04) * mm});
            skLineSegment(sketch, "E102.bottom", {"start": v(-10, -55.04) * mm, "end": v(-46, -55.04) * mm});
            skLineSegment(sketch, "E102.top", {"start": v(-31, -11.04) * mm, "end": v(-46, -11.04) * mm});
            skLineSegment(sketch, "E102.left", {"start": v(-10, -55.04) * mm, "end": v(-10, -11.04) * mm});
            skLineSegment(sketch, "E102.right", {"start": v(-46, -34.04) * mm, "end": v(-46, -11.04) * mm});
            skLineSegment(sketch, "E103.top", {"start": v(-10, 19.96) * mm, "end": v(-31, 19.96) * mm});
            skLineSegment(sketch, "E103.left", {"start": v(-10, -11.04) * mm, "end": v(-10, 19.96) * mm});
            skLineSegment(sketch, "E103.right", {"start": v(-31, -11.04) * mm, "end": v(-31, 19.96) * mm});
            skSolve(sketch);
        }
        {
            var Q0;
            Q0=qSketchRegion(id+"F22",true);
            extrude(context, id + "F23", {"entities" : qUnion([Q0]), "operationType" : NewBodyOperationType.REMOVE, "depth" : 5 * mm});
        }
        {
            var Q0;
            Q0=makeQuery(id+"F23.boolean.opBoolean","COPY",FACE,{"derivedFrom":makeQuery(id+"F23.opExtrude","CAP_FACE",FACE,{"disambiguationData":[OSD([sQuery(id+"F22.wireOp",EDGE,"E101.bottom"),sQuery(id+"F22.wireOp",EDGE,"E101.top"),sQuery(id+"F22.wireOp",EDGE,"E101.left"),sQuery(id+"F22.wireOp",EDGE,"E102.bottom"),sQuery(id+"F22.wireOp",EDGE,"E102.top"),sQuery(id+"F22.wireOp",EDGE,"E102.left"),sQuery(id+"F22.wireOp",EDGE,"E102.right"),sQuery(id+"F22.wireOp",EDGE,"E103.top"),sQuery(id+"F22.wireOp",EDGE,"E103.left"),sQuery(id+"F22.wireOp",EDGE,"E103.right")])],"isStart":false})});
            var sketch = newSketch(context, id + "F24", { "sketchPlane" : qUnion([Q0])});
            skLineSegment(sketch, "E104.bottom", {"start": v(-155, 55.04) * mm, "end": v(-153, 55.04) * mm});
            skLineSegment(sketch, "E104.top", {"start": v(-155, 34.04) * mm, "end": v(-153, 34.04) * mm});
            skLineSegment(sketch, "E104.left", {"start": v(-155, 55.04) * mm, "end": v(-155, 34.04) * mm});
            skLineSegment(sketch, "E104.right", {"start": v(-153, 55.04) * mm, "end": v(-153, 34.04) * mm});
            skLineSegment(sketch, "E105.bottom", {"start": v(-153, 55.04) * mm, "end": v(-10, 55.04) * mm});
            skLineSegment(sketch, "E105.top", {"start": v(-153, 53.04) * mm, "end": v(-10, 53.04) * mm});
            skLineSegment(sketch, "E105.left", {"start": v(-153, 55.04) * mm, "end": v(-153, 53.04) * mm});
            skLineSegment(sketch, "E105.right", {"start": v(-10, 55.04) * mm, "end": v(-10, 53.04) * mm});
            skLineSegment(sketch, "E106.bottom", {"start": v(-10, -19.96) * mm, "end": v(-12, -19.96) * mm});
            skLineSegment(sketch, "E106.top", {"start": v(-10, 53.04) * mm, "end": v(-12, 53.04) * mm});
            skLineSegment(sketch, "E106.left", {"start": v(-10, -19.96) * mm, "end": v(-10, 53.04) * mm});
            skLineSegment(sketch, "E106.right", {"start": v(-12, -19.96) * mm, "end": v(-12, 53.04) * mm});
            skLineSegment(sketch, "E107.bottom", {"start": v(-31, -19.96) * mm, "end": v(-12, -19.96) * mm});
            skLineSegment(sketch, "E107.top", {"start": v(-31, -17.96) * mm, "end": v(-12, -17.96) * mm});
            skLineSegment(sketch, "E107.left", {"start": v(-31, -19.96) * mm, "end": v(-31, -17.96) * mm});
            skLineSegment(sketch, "E107.right", {"start": v(-12, -19.96) * mm, "end": v(-12, -17.96) * mm});
            skLineSegment(sketch, "E108.bottom", {"start": v(-46, 34.04) * mm, "end": v(-12, 34.04) * mm});
            skLineSegment(sketch, "E108.top", {"start": v(-46, 32.04) * mm, "end": v(-12, 32.04) * mm});
            skLineSegment(sketch, "E108.left", {"start": v(-46, 34.04) * mm, "end": v(-46, 32.04) * mm});
            skLineSegment(sketch, "E108.right", {"start": v(-12, 34.04) * mm, "end": v(-12, 32.04) * mm});
            skSolve(sketch);
        }
        {
            var Q0;
            Q0=qSketchRegion(id+"F24",true);
            extrude(context, id + "F25", {"entities" : qUnion([Q0]), "operationType" : NewBodyOperationType.ADD, "depth" : 5 * mm});
        }
    });
